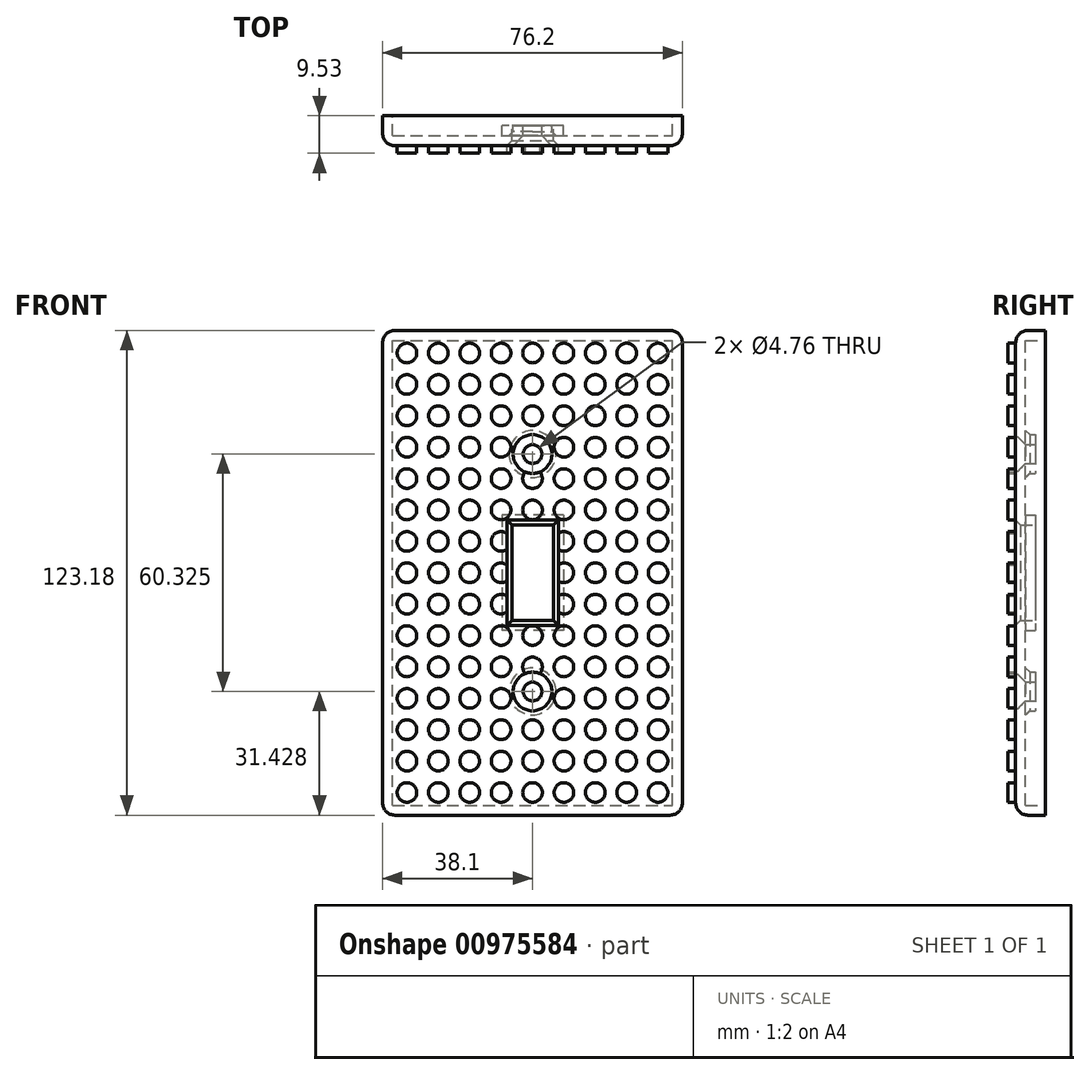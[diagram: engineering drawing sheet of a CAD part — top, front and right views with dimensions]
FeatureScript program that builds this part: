
annotation { "Feature Type Name" : "Feature", "Feature Type Description" : "" }
export const myFeature = defineFeature(function(context is Context, id is Id, definition is map)
    precondition{}
    {
        {
            var Q0;
            Q0=qCreatedBy(makeId("Front.planeOp"),FACE);
            var sketch = newSketch(context, id + "F0", { "sketchPlane" : qUnion([Q0])});
            skLineSegment(sketch, "E0.bottom", {"start": v(-38.1, -61.6) * mm, "end": v(38.1, -61.6) * mm});
            skLineSegment(sketch, "E0.top", {"start": v(-38.1, 61.6) * mm, "end": v(38.1, 61.6) * mm});
            skLineSegment(sketch, "E0.left", {"start": v(-38.1, -61.6) * mm, "end": v(-38.1, 61.6) * mm});
            skLineSegment(sketch, "E0.right", {"start": v(38.1, -61.6) * mm, "end": v(38.1, 61.6) * mm});
            skPoint(sketch, "E0.middle", {"position": v(0, 0) * mm});
            skLineSegment(sketch, "E1", {"start": v(0, 61.6) * mm, "end": v(0, -61.6) * mm, "construction": true});
            skLineSegment(sketch, "E2", {"start": v(-38.1, 0) * mm, "end": v(38.1, 0) * mm, "construction": true});
            skLineSegment(sketch, "E3", {"start": v(22.96, 61.6) * mm, "end": v(22.96, -61.6) * mm, "construction": true});
            skPoint(sketch, "E4.middle", {"position": v(22.96, 0) * mm});
            skLineSegment(sketch, "E5.bottom", {"start": v(-5.27, -12.13) * mm, "end": v(5.27, -12.13) * mm});
            skLineSegment(sketch, "E5.top", {"start": v(-5.27, 12.13) * mm, "end": v(5.27, 12.13) * mm});
            skLineSegment(sketch, "E5.left", {"start": v(-5.27, -12.13) * mm, "end": v(-5.27, 12.13) * mm});
            skLineSegment(sketch, "E5.right", {"start": v(5.27, -12.13) * mm, "end": v(5.27, 12.13) * mm});
            skCircle(sketch, "E6", {"center": v(0, -30.16) * mm, "radius": 2.38 * mm});
            skCircle(sketch, "E7.MirrorC", {"center": v(0, 30.16) * mm, "radius": 2.38 * mm});
            skSolve(sketch);
        }
        {
            var Q0;
            Q0=makeQuery(id+"F0.imprint","IMPRINT",FACE,{"disambiguationData":[TD([[makeQuery(id+"F0.imprint","IMPRINT",EDGE,{"derivedFrom":sQuery(id+"F0.wireOp",EDGE,"E0.bottom")}),1.0]])]});
            extrude(context, id + "F1", {"entities" : qUnion([Q0]), "depth" : 7.62 * mm, "offsetDistance" : 25.4 * mm});
        }
        {
            var Q0;
            Q0=makeQuery(id+"F1.opExtrude","CAP_EDGE",EDGE,{"disambiguationData":[OSD([sQuery(id+"F0.wireOp",EDGE,"E7.MirrorC")])],"isStart":false});
            var Q1;
            Q1=makeQuery(id+"F1.opExtrude","CAP_EDGE",EDGE,{"disambiguationData":[OSD([sQuery(id+"F0.wireOp",EDGE,"E6")])],"isStart":false});
            chamfer(context, id + "F2", {"entities" : qUnion([Q0, Q1]), "width" : 2.54 * mm, "tangentPropagation" : true});
        }
        {
            var Q0;
            Q0=makeQuery(id+"F1.opExtrude","CAP_EDGE",EDGE,{"disambiguationData":[OSD([sQuery(id+"F0.wireOp",EDGE,"E5.bottom")])],"isStart":false});
            var Q1;
            Q1=makeQuery(id+"F1.opExtrude","CAP_EDGE",EDGE,{"disambiguationData":[OSD([sQuery(id+"F0.wireOp",EDGE,"E5.top")])],"isStart":false});
            var Q2;
            Q2=makeQuery(id+"F1.opExtrude","CAP_EDGE",EDGE,{"disambiguationData":[OSD([sQuery(id+"F0.wireOp",EDGE,"E5.right")])],"isStart":false});
            var Q3;
            Q3=makeQuery(id+"F1.opExtrude","CAP_EDGE",EDGE,{"disambiguationData":[OSD([sQuery(id+"F0.wireOp",EDGE,"E5.left")])],"isStart":false});
            chamfer(context, id + "F3", {"entities" : qUnion([Q0, Q1, Q2, Q3]), "width" : 1.27 * mm, "tangentPropagation" : true});
        }
        {
            var Q0;
            Q0=makeQuery(id+"F1.opExtrude","CAP_FACE",FACE,{"disambiguationData":[OSD([sQuery(id+"F0.wireOp",EDGE,"E0.bottom"),sQuery(id+"F0.wireOp",EDGE,"E0.top"),sQuery(id+"F0.wireOp",EDGE,"E0.left"),sQuery(id+"F0.wireOp",EDGE,"E0.right"),sQuery(id+"F0.wireOp",EDGE,"E4.bottom"),sQuery(id+"F0.wireOp",EDGE,"E4.top"),sQuery(id+"F0.wireOp",EDGE,"E4.left"),sQuery(id+"F0.wireOp",EDGE,"E4.right"),sQuery(id+"F0.wireOp",EDGE,"S8rWea5z-x2db-HdL8-dZlx-mBKRZtJuW5yt"),sQuery(id+"F0.wireOp",EDGE,"667eedda-f1dc-4c61-957f-706faf60f5200.MirrorC"),sQuery(id+"F0.wireOp",EDGE,"48815ae1-3f2c-4afa-9184-387e88e8cfc90.MirrorC"),sQuery(id+"F0.wireOp",EDGE,"5efa72a1-dbf9-4033-b1ce-7067f076b67a0.MirrorC"),sQuery(id+"F0.wireOp",EDGE,"e74374d9-3310-4d52-b099-d9de6480f7030.MirrorCS"),sQuery(id+"F0.wireOp",EDGE,"54ec0b88-7cfc-4447-87f8-6753f306d23d0.MirrorCS"),sQuery(id+"F0.wireOp",EDGE,"b89ad579-1ec3-48bc-a1ee-9315b749428f0.MirrorCS"),sQuery(id+"F0.wireOp",EDGE,"6356497d-8d2b-4f01-b385-a6d8bf8b30600.MirrorCS")])],"isStart":true});
            shell(context, id + "F4", {"entities" : qUnion([Q0]), "thickness" : 2.54 * mm});
        }
        {
            var Q0;
            {var subQ0=sQuery(id+"F0.wireOp",EDGE,"6356497d-8d2b-4f01-b385-a6d8bf8b30600.MirrorCS");var subQ1=sQuery(id+"F0.wireOp",EDGE,"b89ad579-1ec3-48bc-a1ee-9315b749428f0.MirrorCS");var subQ2=sQuery(id+"F0.wireOp",EDGE,"54ec0b88-7cfc-4447-87f8-6753f306d23d0.MirrorCS");var subQ3=sQuery(id+"F0.wireOp",EDGE,"e74374d9-3310-4d52-b099-d9de6480f7030.MirrorCS");var subQ4=sQuery(id+"F0.wireOp",EDGE,"5efa72a1-dbf9-4033-b1ce-7067f076b67a0.MirrorC");var subQ5=sQuery(id+"F0.wireOp",EDGE,"48815ae1-3f2c-4afa-9184-387e88e8cfc90.MirrorC");var subQ6=sQuery(id+"F0.wireOp",EDGE,"667eedda-f1dc-4c61-957f-706faf60f5200.MirrorC");var subQ7=sQuery(id+"F0.wireOp",EDGE,"S8rWea5z-x2db-HdL8-dZlx-mBKRZtJuW5yt");var subQ8=sQuery(id+"F0.wireOp",EDGE,"E4.right");var subQ9=sQuery(id+"F0.wireOp",EDGE,"E4.left");var subQ10=sQuery(id+"F0.wireOp",EDGE,"E4.top");var subQ11=sQuery(id+"F0.wireOp",EDGE,"E4.bottom");var subQ12=sQuery(id+"F0.wireOp",EDGE,"E0.right");var subQ13=sQuery(id+"F0.wireOp",EDGE,"E0.left");var subQ14=sQuery(id+"F0.wireOp",EDGE,"E0.top");var subQ15=sQuery(id+"F0.wireOp",EDGE,"E0.bottom");Q0=makeQuery(id+"F4.opShell","OFFSET_FACE",FACE,{"disambiguationData":[OSD([subQ15,subQ14,subQ13,subQ12,subQ11,subQ10,subQ9,subQ8,subQ7,subQ6,subQ5,subQ4,subQ3,subQ2,subQ1,subQ0]),TDD([makeQuery(id+"F1.opExtrude","CAP_FACE",FACE,{"disambiguationData":[OSD([subQ15,subQ14,subQ13,subQ12,subQ11,subQ10,subQ9,subQ8,subQ7,subQ6,subQ5,subQ4,subQ3,subQ2,subQ1,subQ0])],"isStart":true})]),OD(0.0)]});}
            var sketch = newSketch(context, id + "F5", { "sketchPlane" : qUnion([Q0])});
            skLineSegment(sketch, "E8.bottom", {"start": v(-28.58, -38.1) * mm, "end": v(28.58, -38.1) * mm});
            skLineSegment(sketch, "E8.top", {"start": v(-28.58, 38.1) * mm, "end": v(28.57, 38.1) * mm});
            skLineSegment(sketch, "E8.left", {"start": v(-28.58, -38.1) * mm, "end": v(-28.58, 38.1) * mm});
            skLineSegment(sketch, "E8.right", {"start": v(28.58, -38.1) * mm, "end": v(28.57, 38.1) * mm});
            skPoint(sketch, "E8.middle", {"position": v(0, 0) * mm});
            skSolve(sketch);
        }
        {
            var Q0;
            Q0=makeQuery(id+"F5.imprint","IMPRINT",FACE,{"disambiguationData":[TD([[makeQuery(id+"F5.imprint","IMPRINT",EDGE,{"derivedFrom":sQuery(id+"F5.wireOp",EDGE,"E8.bottom")}),1.0]])]});
            extrude(context, id + "F6", {"entities" : qUnion([Q0]), "operationType" : NewBodyOperationType.REMOVE, "oppositeDirection" : true, "depth" : 2.54 * mm, "offsetDistance" : 25.4 * mm});
        }
        {
            var Q0;
            Q0=makeQuery(id+"F1.opExtrude","SWEPT_EDGE",EDGE,{"disambiguationData":[OSD([sQuery(id+"F0.wireOp",EDGE,"E0.top"),sQuery(id+"F0.wireOp",EDGE,"E0.right")])]});
            var Q1;
            Q1=makeQuery(id+"F1.opExtrude","SWEPT_EDGE",EDGE,{"disambiguationData":[OSD([sQuery(id+"F0.wireOp",EDGE,"E0.bottom"),sQuery(id+"F0.wireOp",EDGE,"E0.right")])]});
            var Q2;
            Q2=makeQuery(id+"F1.opExtrude","SWEPT_EDGE",EDGE,{"disambiguationData":[OSD([sQuery(id+"F0.wireOp",EDGE,"E0.bottom"),sQuery(id+"F0.wireOp",EDGE,"E0.left")])]});
            var Q3;
            Q3=makeQuery(id+"F1.opExtrude","SWEPT_EDGE",EDGE,{"disambiguationData":[OSD([sQuery(id+"F0.wireOp",EDGE,"E0.top"),sQuery(id+"F0.wireOp",EDGE,"E0.left")])]});
            fillet(context, id + "F7", {"entities" : qUnion([Q0, Q1, Q2, Q3]), "radius" : 3.17 * mm, "tangentPropagation" : true, "allowEdgeOverflow" : false});
        }
        {
            var Q0;
            Q0=makeQuery(id+"F1.opExtrude","CAP_EDGE",EDGE,{"disambiguationData":[OSD([sQuery(id+"F0.wireOp",EDGE,"E0.top")])],"isStart":false});
            fillet(context, id + "F8", {"entities" : qUnion([Q0]), "radius" : 3.17 * mm, "tangentPropagation" : true, "allowEdgeOverflow" : false});
        }
        {
            var Q0;
            Q0=makeQuery(id+"F1.opExtrude","CAP_FACE",FACE,{"disambiguationData":[OSD([sQuery(id+"F0.wireOp",EDGE,"E0.bottom"),sQuery(id+"F0.wireOp",EDGE,"E0.top"),sQuery(id+"F0.wireOp",EDGE,"E0.left"),sQuery(id+"F0.wireOp",EDGE,"E0.right"),sQuery(id+"F0.wireOp",EDGE,"E5.bottom"),sQuery(id+"F0.wireOp",EDGE,"E5.top"),sQuery(id+"F0.wireOp",EDGE,"E5.left"),sQuery(id+"F0.wireOp",EDGE,"E5.right"),sQuery(id+"F0.wireOp",EDGE,"E6"),sQuery(id+"F0.wireOp",EDGE,"E7.MirrorC")])],"isStart":false});
            var sketch = newSketch(context, id + "F9", { "sketchPlane" : qUnion([Q0])});
            skCircle(sketch, "E9", {"center": v(0, 0) * mm, "radius": 2.49 * mm, "construction": true});
            skCircle(sketch, "E10.0.2.0", {"center": v(0, 15.95) * mm, "radius": 2.49 * mm});
            skCircle(sketch, "E10.0.3.0", {"center": v(0, 23.93) * mm, "radius": 2.49 * mm});
            skCircle(sketch, "E10.0.5.0", {"center": v(0, 39.88) * mm, "radius": 2.49 * mm});
            skCircle(sketch, "E10.0.6.0", {"center": v(0, 47.85) * mm, "radius": 2.49 * mm});
            skCircle(sketch, "E10.0.7.0", {"center": v(0, 55.83) * mm, "radius": 2.49 * mm});
            skCircle(sketch, "E10.1.0.0", {"center": v(7.98, 0) * mm, "radius": 2.49 * mm});
            skCircle(sketch, "E10.1.1.0", {"center": v(7.98, 7.98) * mm, "radius": 2.49 * mm});
            skCircle(sketch, "E10.1.2.0", {"center": v(7.98, 15.95) * mm, "radius": 2.49 * mm});
            skCircle(sketch, "E10.1.3.0", {"center": v(7.98, 23.93) * mm, "radius": 2.49 * mm});
            skCircle(sketch, "E10.1.4.0", {"center": v(7.98, 31.9) * mm, "radius": 2.49 * mm});
            skCircle(sketch, "E10.1.5.0", {"center": v(7.98, 39.88) * mm, "radius": 2.49 * mm});
            skCircle(sketch, "E10.1.6.0", {"center": v(7.98, 47.85) * mm, "radius": 2.49 * mm});
            skCircle(sketch, "E10.1.7.0", {"center": v(7.98, 55.83) * mm, "radius": 2.49 * mm});
            skCircle(sketch, "E10.2.0.0", {"center": v(15.95, 0) * mm, "radius": 2.49 * mm});
            skCircle(sketch, "E10.2.1.0", {"center": v(15.95, 7.98) * mm, "radius": 2.49 * mm});
            skCircle(sketch, "E10.2.2.0", {"center": v(15.95, 15.95) * mm, "radius": 2.49 * mm});
            skCircle(sketch, "E10.2.3.0", {"center": v(15.95, 23.93) * mm, "radius": 2.49 * mm});
            skCircle(sketch, "E10.2.4.0", {"center": v(15.95, 31.9) * mm, "radius": 2.49 * mm});
            skCircle(sketch, "E10.2.5.0", {"center": v(15.95, 39.88) * mm, "radius": 2.49 * mm});
            skCircle(sketch, "E10.2.6.0", {"center": v(15.95, 47.85) * mm, "radius": 2.49 * mm});
            skCircle(sketch, "E10.2.7.0", {"center": v(15.95, 55.83) * mm, "radius": 2.49 * mm});
            skCircle(sketch, "E10.3.0.0", {"center": v(23.93, 0) * mm, "radius": 2.49 * mm});
            skCircle(sketch, "E10.3.1.0", {"center": v(23.93, 7.98) * mm, "radius": 2.49 * mm});
            skCircle(sketch, "E10.3.2.0", {"center": v(23.93, 15.95) * mm, "radius": 2.49 * mm});
            skCircle(sketch, "E10.3.3.0", {"center": v(23.93, 23.93) * mm, "radius": 2.49 * mm});
            skCircle(sketch, "E10.3.4.0", {"center": v(23.93, 31.9) * mm, "radius": 2.49 * mm});
            skCircle(sketch, "E10.3.5.0", {"center": v(23.93, 39.88) * mm, "radius": 2.49 * mm});
            skCircle(sketch, "E10.3.6.0", {"center": v(23.93, 47.85) * mm, "radius": 2.49 * mm});
            skCircle(sketch, "E10.3.7.0", {"center": v(23.93, 55.83) * mm, "radius": 2.49 * mm});
            skCircle(sketch, "E10.4.0.0", {"center": v(31.9, 0) * mm, "radius": 2.49 * mm});
            skCircle(sketch, "E10.4.1.0", {"center": v(31.9, 7.98) * mm, "radius": 2.49 * mm});
            skCircle(sketch, "E10.4.2.0", {"center": v(31.9, 15.95) * mm, "radius": 2.49 * mm});
            skCircle(sketch, "E10.4.3.0", {"center": v(31.9, 23.93) * mm, "radius": 2.49 * mm});
            skCircle(sketch, "E10.4.4.0", {"center": v(31.9, 31.9) * mm, "radius": 2.49 * mm});
            skCircle(sketch, "E10.4.5.0", {"center": v(31.9, 39.88) * mm, "radius": 2.49 * mm});
            skCircle(sketch, "E10.4.6.0", {"center": v(31.9, 47.85) * mm, "radius": 2.49 * mm});
            skCircle(sketch, "E10.4.7.0", {"center": v(31.9, 55.83) * mm, "radius": 2.49 * mm});
            skLineSegment(sketch, "E10.direction1", {"start": v(0, 0) * mm, "end": v(7.98, 0) * mm, "construction": true});
            skLineSegment(sketch, "E10.direction2", {"start": v(0, 0) * mm, "end": v(0, 7.98) * mm, "construction": true});
            skCircle(sketch, "E11.0.1.0", {"center": v(-7.98, 0) * mm, "radius": 2.49 * mm});
            skCircle(sketch, "E11.0.2.0", {"center": v(-15.95, 0) * mm, "radius": 2.49 * mm});
            skCircle(sketch, "E11.0.3.0", {"center": v(-23.93, 0) * mm, "radius": 2.49 * mm});
            skCircle(sketch, "E11.0.4.0", {"center": v(-31.9, 0) * mm, "radius": 2.49 * mm});
            skCircle(sketch, "E11.1.1.0", {"center": v(-7.98, -7.98) * mm, "radius": 2.49 * mm});
            skCircle(sketch, "E11.1.2.0", {"center": v(-15.95, -7.98) * mm, "radius": 2.49 * mm});
            skCircle(sketch, "E11.1.3.0", {"center": v(-23.93, -7.98) * mm, "radius": 2.49 * mm});
            skCircle(sketch, "E11.1.4.0", {"center": v(-31.9, -7.98) * mm, "radius": 2.49 * mm});
            skCircle(sketch, "E11.2.0.0", {"center": v(0, -15.95) * mm, "radius": 2.49 * mm});
            skCircle(sketch, "E11.2.1.0", {"center": v(-7.98, -15.95) * mm, "radius": 2.49 * mm});
            skCircle(sketch, "E11.2.2.0", {"center": v(-15.95, -15.95) * mm, "radius": 2.49 * mm});
            skCircle(sketch, "E11.2.3.0", {"center": v(-23.93, -15.95) * mm, "radius": 2.49 * mm});
            skCircle(sketch, "E11.2.4.0", {"center": v(-31.9, -15.95) * mm, "radius": 2.49 * mm});
            skCircle(sketch, "E11.3.0.0", {"center": v(0, -23.93) * mm, "radius": 2.49 * mm});
            skCircle(sketch, "E11.3.1.0", {"center": v(-7.98, -23.93) * mm, "radius": 2.49 * mm});
            skCircle(sketch, "E11.3.2.0", {"center": v(-15.95, -23.93) * mm, "radius": 2.49 * mm});
            skCircle(sketch, "E11.3.3.0", {"center": v(-23.93, -23.93) * mm, "radius": 2.49 * mm});
            skCircle(sketch, "E11.3.4.0", {"center": v(-31.9, -23.93) * mm, "radius": 2.49 * mm});
            skCircle(sketch, "E11.4.1.0", {"center": v(-7.98, -31.9) * mm, "radius": 2.49 * mm});
            skCircle(sketch, "E11.4.2.0", {"center": v(-15.95, -31.9) * mm, "radius": 2.49 * mm});
            skCircle(sketch, "E11.4.3.0", {"center": v(-23.93, -31.9) * mm, "radius": 2.49 * mm});
            skCircle(sketch, "E11.4.4.0", {"center": v(-31.9, -31.9) * mm, "radius": 2.49 * mm});
            skCircle(sketch, "E11.5.0.0", {"center": v(0, -39.88) * mm, "radius": 2.49 * mm});
            skCircle(sketch, "E11.5.1.0", {"center": v(-7.98, -39.88) * mm, "radius": 2.49 * mm});
            skCircle(sketch, "E11.5.2.0", {"center": v(-15.95, -39.88) * mm, "radius": 2.49 * mm});
            skCircle(sketch, "E11.5.3.0", {"center": v(-23.93, -39.88) * mm, "radius": 2.49 * mm});
            skCircle(sketch, "E11.5.4.0", {"center": v(-31.9, -39.88) * mm, "radius": 2.49 * mm});
            skCircle(sketch, "E11.6.0.0", {"center": v(0, -47.85) * mm, "radius": 2.49 * mm});
            skCircle(sketch, "E11.6.1.0", {"center": v(-7.98, -47.85) * mm, "radius": 2.49 * mm});
            skCircle(sketch, "E11.6.2.0", {"center": v(-15.95, -47.85) * mm, "radius": 2.49 * mm});
            skCircle(sketch, "E11.6.3.0", {"center": v(-23.93, -47.85) * mm, "radius": 2.49 * mm});
            skCircle(sketch, "E11.6.4.0", {"center": v(-31.9, -47.85) * mm, "radius": 2.49 * mm});
            skCircle(sketch, "E11.7.0.0", {"center": v(0, -55.83) * mm, "radius": 2.49 * mm});
            skCircle(sketch, "E11.7.1.0", {"center": v(-7.98, -55.83) * mm, "radius": 2.49 * mm});
            skCircle(sketch, "E11.7.2.0", {"center": v(-15.95, -55.83) * mm, "radius": 2.49 * mm});
            skCircle(sketch, "E11.7.3.0", {"center": v(-23.93, -55.83) * mm, "radius": 2.49 * mm});
            skCircle(sketch, "E11.7.4.0", {"center": v(-31.9, -55.83) * mm, "radius": 2.49 * mm});
            skLineSegment(sketch, "E11.direction1", {"start": v(0, 0) * mm, "end": v(0, -7.98) * mm, "construction": true});
            skLineSegment(sketch, "E11.direction2", {"start": v(0, 0) * mm, "end": v(-7.98, 0) * mm, "construction": true});
            skCircle(sketch, "E12.1.1.0", {"center": v(-7.98, 7.98) * mm, "radius": 2.49 * mm});
            skCircle(sketch, "E12.1.2.0", {"center": v(-7.98, 15.95) * mm, "radius": 2.49 * mm});
            skCircle(sketch, "E12.1.3.0", {"center": v(-7.98, 23.93) * mm, "radius": 2.49 * mm});
            skCircle(sketch, "E12.1.4.0", {"center": v(-7.98, 31.9) * mm, "radius": 2.49 * mm});
            skCircle(sketch, "E12.1.5.0", {"center": v(-7.98, 39.88) * mm, "radius": 2.49 * mm});
            skCircle(sketch, "E12.1.6.0", {"center": v(-7.98, 47.85) * mm, "radius": 2.49 * mm});
            skCircle(sketch, "E12.1.7.0", {"center": v(-7.98, 55.83) * mm, "radius": 2.49 * mm});
            skCircle(sketch, "E12.2.1.0", {"center": v(-15.95, 7.98) * mm, "radius": 2.49 * mm});
            skCircle(sketch, "E12.2.2.0", {"center": v(-15.95, 15.95) * mm, "radius": 2.49 * mm});
            skCircle(sketch, "E12.2.3.0", {"center": v(-15.95, 23.93) * mm, "radius": 2.49 * mm});
            skCircle(sketch, "E12.2.4.0", {"center": v(-15.95, 31.9) * mm, "radius": 2.49 * mm});
            skCircle(sketch, "E12.2.5.0", {"center": v(-15.95, 39.88) * mm, "radius": 2.49 * mm});
            skCircle(sketch, "E12.2.6.0", {"center": v(-15.95, 47.85) * mm, "radius": 2.49 * mm});
            skCircle(sketch, "E12.2.7.0", {"center": v(-15.95, 55.83) * mm, "radius": 2.49 * mm});
            skCircle(sketch, "E12.3.1.0", {"center": v(-23.93, 7.98) * mm, "radius": 2.49 * mm});
            skCircle(sketch, "E12.3.2.0", {"center": v(-23.93, 15.95) * mm, "radius": 2.49 * mm});
            skCircle(sketch, "E12.3.3.0", {"center": v(-23.93, 23.93) * mm, "radius": 2.49 * mm});
            skCircle(sketch, "E12.3.4.0", {"center": v(-23.93, 31.9) * mm, "radius": 2.49 * mm});
            skCircle(sketch, "E12.3.5.0", {"center": v(-23.93, 39.88) * mm, "radius": 2.49 * mm});
            skCircle(sketch, "E12.3.6.0", {"center": v(-23.93, 47.85) * mm, "radius": 2.49 * mm});
            skCircle(sketch, "E12.3.7.0", {"center": v(-23.93, 55.83) * mm, "radius": 2.49 * mm});
            skCircle(sketch, "E12.4.1.0", {"center": v(-31.9, 7.98) * mm, "radius": 2.49 * mm});
            skCircle(sketch, "E12.4.2.0", {"center": v(-31.9, 15.95) * mm, "radius": 2.49 * mm});
            skCircle(sketch, "E12.4.3.0", {"center": v(-31.9, 23.93) * mm, "radius": 2.49 * mm});
            skCircle(sketch, "E12.4.4.0", {"center": v(-31.9, 31.9) * mm, "radius": 2.49 * mm});
            skCircle(sketch, "E12.4.5.0", {"center": v(-31.9, 39.88) * mm, "radius": 2.49 * mm});
            skCircle(sketch, "E12.4.6.0", {"center": v(-31.9, 47.85) * mm, "radius": 2.49 * mm});
            skCircle(sketch, "E12.4.7.0", {"center": v(-31.9, 55.83) * mm, "radius": 2.49 * mm});
            skCircle(sketch, "E13.1.1.0", {"center": v(7.98, -7.98) * mm, "radius": 2.49 * mm});
            skCircle(sketch, "E13.1.2.0", {"center": v(7.98, -15.95) * mm, "radius": 2.49 * mm});
            skCircle(sketch, "E13.1.3.0", {"center": v(7.98, -23.93) * mm, "radius": 2.49 * mm});
            skCircle(sketch, "E13.1.4.0", {"center": v(7.98, -31.9) * mm, "radius": 2.49 * mm});
            skCircle(sketch, "E13.1.5.0", {"center": v(7.98, -39.88) * mm, "radius": 2.49 * mm});
            skCircle(sketch, "E13.1.6.0", {"center": v(7.98, -47.85) * mm, "radius": 2.49 * mm});
            skCircle(sketch, "E13.1.7.0", {"center": v(7.98, -55.83) * mm, "radius": 2.49 * mm});
            skCircle(sketch, "E13.2.1.0", {"center": v(15.95, -7.98) * mm, "radius": 2.49 * mm});
            skCircle(sketch, "E13.2.2.0", {"center": v(15.95, -15.95) * mm, "radius": 2.49 * mm});
            skCircle(sketch, "E13.2.3.0", {"center": v(15.95, -23.93) * mm, "radius": 2.49 * mm});
            skCircle(sketch, "E13.2.4.0", {"center": v(15.95, -31.9) * mm, "radius": 2.49 * mm});
            skCircle(sketch, "E13.2.5.0", {"center": v(15.95, -39.88) * mm, "radius": 2.49 * mm});
            skCircle(sketch, "E13.2.6.0", {"center": v(15.95, -47.85) * mm, "radius": 2.49 * mm});
            skCircle(sketch, "E13.2.7.0", {"center": v(15.95, -55.83) * mm, "radius": 2.49 * mm});
            skCircle(sketch, "E13.3.1.0", {"center": v(23.93, -7.98) * mm, "radius": 2.49 * mm});
            skCircle(sketch, "E13.3.2.0", {"center": v(23.93, -15.95) * mm, "radius": 2.49 * mm});
            skCircle(sketch, "E13.3.3.0", {"center": v(23.93, -23.93) * mm, "radius": 2.49 * mm});
            skCircle(sketch, "E13.3.4.0", {"center": v(23.93, -31.9) * mm, "radius": 2.49 * mm});
            skCircle(sketch, "E13.3.5.0", {"center": v(23.93, -39.88) * mm, "radius": 2.49 * mm});
            skCircle(sketch, "E13.3.6.0", {"center": v(23.93, -47.85) * mm, "radius": 2.49 * mm});
            skCircle(sketch, "E13.3.7.0", {"center": v(23.93, -55.83) * mm, "radius": 2.49 * mm});
            skCircle(sketch, "E13.4.1.0", {"center": v(31.9, -7.98) * mm, "radius": 2.49 * mm});
            skCircle(sketch, "E13.4.2.0", {"center": v(31.9, -15.95) * mm, "radius": 2.49 * mm});
            skCircle(sketch, "E13.4.3.0", {"center": v(31.9, -23.93) * mm, "radius": 2.49 * mm});
            skCircle(sketch, "E13.4.4.0", {"center": v(31.9, -31.9) * mm, "radius": 2.49 * mm});
            skCircle(sketch, "E13.4.5.0", {"center": v(31.9, -39.88) * mm, "radius": 2.49 * mm});
            skCircle(sketch, "E13.4.6.0", {"center": v(31.9, -47.85) * mm, "radius": 2.49 * mm});
            skCircle(sketch, "E13.4.7.0", {"center": v(31.9, -55.83) * mm, "radius": 2.49 * mm});
            skSolve(sketch);
        }
        {
            var Q0;
            {var subQ0=sQuery(id+"F9.wireOp",EDGE,"E12.4.7.0");var subQ1=sQuery(id+"F0.wireOp",EDGE,"E0.left");var subQ2=makeQuery(id+"F8.opFillet","BLEND_EDGE",EDGE,{"blendedFrom":[makeQuery(id+"F1.opExtrude","CAP_EDGE",EDGE,{"disambiguationData":[OSD([subQ1])],"isStart":false}),makeQuery(id+"F1.opExtrude","CAP_FACE",FACE,{"disambiguationData":[OSD([sQuery(id+"F0.wireOp",EDGE,"E0.bottom"),sQuery(id+"F0.wireOp",EDGE,"E0.top"),subQ1,sQuery(id+"F0.wireOp",EDGE,"E0.right"),sQuery(id+"F0.wireOp",EDGE,"E5.bottom"),sQuery(id+"F0.wireOp",EDGE,"E5.top"),sQuery(id+"F0.wireOp",EDGE,"E5.left"),sQuery(id+"F0.wireOp",EDGE,"E5.right"),sQuery(id+"F0.wireOp",EDGE,"E6"),sQuery(id+"F0.wireOp",EDGE,"E7.MirrorC")])],"isStart":false})],"blendedInto":[makeQuery(id+"F1.opExtrude","CAP_FACE",FACE,{"disambiguationData":[OSD([sQuery(id+"F0.wireOp",EDGE,"E0.bottom"),sQuery(id+"F0.wireOp",EDGE,"E0.top"),subQ1,sQuery(id+"F0.wireOp",EDGE,"E0.right"),sQuery(id+"F0.wireOp",EDGE,"E5.bottom"),sQuery(id+"F0.wireOp",EDGE,"E5.top"),sQuery(id+"F0.wireOp",EDGE,"E5.left"),sQuery(id+"F0.wireOp",EDGE,"E5.right"),sQuery(id+"F0.wireOp",EDGE,"E6"),sQuery(id+"F0.wireOp",EDGE,"E7.MirrorC")])],"isStart":false})]});var subQ3=makeQuery(id+"F9.imprint","INTERSECT",VERTEX,{"disambiguationData":[OD(0.0)],"derivedFrom":[subQ2,subQ0]});Q0=makeQuery(id+"F9.imprint","IMPRINT",FACE,{"disambiguationData":[TD([[makeQuery(id+"F9.imprint","IMPRINT",EDGE,{"disambiguationData":[TD([[subQ3,1.0]])],"derivedFrom":subQ0}),1.0]])]});}
            var Q1;
            {var subQ0=sQuery(id+"F9.wireOp",EDGE,"E12.4.6.0");var subQ1=sQuery(id+"F0.wireOp",EDGE,"E0.left");var subQ2=makeQuery(id+"F8.opFillet","BLEND_EDGE",EDGE,{"blendedFrom":[makeQuery(id+"F1.opExtrude","CAP_EDGE",EDGE,{"disambiguationData":[OSD([subQ1])],"isStart":false}),makeQuery(id+"F1.opExtrude","CAP_FACE",FACE,{"disambiguationData":[OSD([sQuery(id+"F0.wireOp",EDGE,"E0.bottom"),sQuery(id+"F0.wireOp",EDGE,"E0.top"),subQ1,sQuery(id+"F0.wireOp",EDGE,"E0.right"),sQuery(id+"F0.wireOp",EDGE,"E5.bottom"),sQuery(id+"F0.wireOp",EDGE,"E5.top"),sQuery(id+"F0.wireOp",EDGE,"E5.left"),sQuery(id+"F0.wireOp",EDGE,"E5.right"),sQuery(id+"F0.wireOp",EDGE,"E6"),sQuery(id+"F0.wireOp",EDGE,"E7.MirrorC")])],"isStart":false})],"blendedInto":[makeQuery(id+"F1.opExtrude","CAP_FACE",FACE,{"disambiguationData":[OSD([sQuery(id+"F0.wireOp",EDGE,"E0.bottom"),sQuery(id+"F0.wireOp",EDGE,"E0.top"),subQ1,sQuery(id+"F0.wireOp",EDGE,"E0.right"),sQuery(id+"F0.wireOp",EDGE,"E5.bottom"),sQuery(id+"F0.wireOp",EDGE,"E5.top"),sQuery(id+"F0.wireOp",EDGE,"E5.left"),sQuery(id+"F0.wireOp",EDGE,"E5.right"),sQuery(id+"F0.wireOp",EDGE,"E6"),sQuery(id+"F0.wireOp",EDGE,"E7.MirrorC")])],"isStart":false})]});var subQ3=makeQuery(id+"F9.imprint","INTERSECT",VERTEX,{"disambiguationData":[OD(0.0)],"derivedFrom":[subQ2,subQ0]});Q1=makeQuery(id+"F9.imprint","IMPRINT",FACE,{"disambiguationData":[TD([[makeQuery(id+"F9.imprint","IMPRINT",EDGE,{"disambiguationData":[TD([[subQ3,1.0]])],"derivedFrom":subQ0}),1.0]])]});}
            var Q2;
            {var subQ0=sQuery(id+"F9.wireOp",EDGE,"E12.4.5.0");var subQ1=sQuery(id+"F0.wireOp",EDGE,"E0.left");var subQ2=makeQuery(id+"F8.opFillet","BLEND_EDGE",EDGE,{"blendedFrom":[makeQuery(id+"F1.opExtrude","CAP_EDGE",EDGE,{"disambiguationData":[OSD([subQ1])],"isStart":false}),makeQuery(id+"F1.opExtrude","CAP_FACE",FACE,{"disambiguationData":[OSD([sQuery(id+"F0.wireOp",EDGE,"E0.bottom"),sQuery(id+"F0.wireOp",EDGE,"E0.top"),subQ1,sQuery(id+"F0.wireOp",EDGE,"E0.right"),sQuery(id+"F0.wireOp",EDGE,"E5.bottom"),sQuery(id+"F0.wireOp",EDGE,"E5.top"),sQuery(id+"F0.wireOp",EDGE,"E5.left"),sQuery(id+"F0.wireOp",EDGE,"E5.right"),sQuery(id+"F0.wireOp",EDGE,"E6"),sQuery(id+"F0.wireOp",EDGE,"E7.MirrorC")])],"isStart":false})],"blendedInto":[makeQuery(id+"F1.opExtrude","CAP_FACE",FACE,{"disambiguationData":[OSD([sQuery(id+"F0.wireOp",EDGE,"E0.bottom"),sQuery(id+"F0.wireOp",EDGE,"E0.top"),subQ1,sQuery(id+"F0.wireOp",EDGE,"E0.right"),sQuery(id+"F0.wireOp",EDGE,"E5.bottom"),sQuery(id+"F0.wireOp",EDGE,"E5.top"),sQuery(id+"F0.wireOp",EDGE,"E5.left"),sQuery(id+"F0.wireOp",EDGE,"E5.right"),sQuery(id+"F0.wireOp",EDGE,"E6"),sQuery(id+"F0.wireOp",EDGE,"E7.MirrorC")])],"isStart":false})]});var subQ3=makeQuery(id+"F9.imprint","INTERSECT",VERTEX,{"disambiguationData":[OD(0.0)],"derivedFrom":[subQ2,subQ0]});Q2=makeQuery(id+"F9.imprint","IMPRINT",FACE,{"disambiguationData":[TD([[makeQuery(id+"F9.imprint","IMPRINT",EDGE,{"disambiguationData":[TD([[subQ3,1.0]])],"derivedFrom":subQ0}),1.0]])]});}
            var Q3;
            {var subQ0=sQuery(id+"F9.wireOp",EDGE,"E12.4.4.0");var subQ1=sQuery(id+"F0.wireOp",EDGE,"E0.left");var subQ2=makeQuery(id+"F8.opFillet","BLEND_EDGE",EDGE,{"blendedFrom":[makeQuery(id+"F1.opExtrude","CAP_EDGE",EDGE,{"disambiguationData":[OSD([subQ1])],"isStart":false}),makeQuery(id+"F1.opExtrude","CAP_FACE",FACE,{"disambiguationData":[OSD([sQuery(id+"F0.wireOp",EDGE,"E0.bottom"),sQuery(id+"F0.wireOp",EDGE,"E0.top"),subQ1,sQuery(id+"F0.wireOp",EDGE,"E0.right"),sQuery(id+"F0.wireOp",EDGE,"E5.bottom"),sQuery(id+"F0.wireOp",EDGE,"E5.top"),sQuery(id+"F0.wireOp",EDGE,"E5.left"),sQuery(id+"F0.wireOp",EDGE,"E5.right"),sQuery(id+"F0.wireOp",EDGE,"E6"),sQuery(id+"F0.wireOp",EDGE,"E7.MirrorC")])],"isStart":false})],"blendedInto":[makeQuery(id+"F1.opExtrude","CAP_FACE",FACE,{"disambiguationData":[OSD([sQuery(id+"F0.wireOp",EDGE,"E0.bottom"),sQuery(id+"F0.wireOp",EDGE,"E0.top"),subQ1,sQuery(id+"F0.wireOp",EDGE,"E0.right"),sQuery(id+"F0.wireOp",EDGE,"E5.bottom"),sQuery(id+"F0.wireOp",EDGE,"E5.top"),sQuery(id+"F0.wireOp",EDGE,"E5.left"),sQuery(id+"F0.wireOp",EDGE,"E5.right"),sQuery(id+"F0.wireOp",EDGE,"E6"),sQuery(id+"F0.wireOp",EDGE,"E7.MirrorC")])],"isStart":false})]});var subQ3=makeQuery(id+"F9.imprint","INTERSECT",VERTEX,{"disambiguationData":[OD(0.0)],"derivedFrom":[subQ2,subQ0]});Q3=makeQuery(id+"F9.imprint","IMPRINT",FACE,{"disambiguationData":[TD([[makeQuery(id+"F9.imprint","IMPRINT",EDGE,{"disambiguationData":[TD([[subQ3,1.0]])],"derivedFrom":subQ0}),1.0]])]});}
            var Q4;
            {var subQ0=sQuery(id+"F9.wireOp",EDGE,"E12.4.3.0");var subQ1=sQuery(id+"F0.wireOp",EDGE,"E0.left");var subQ2=makeQuery(id+"F8.opFillet","BLEND_EDGE",EDGE,{"blendedFrom":[makeQuery(id+"F1.opExtrude","CAP_EDGE",EDGE,{"disambiguationData":[OSD([subQ1])],"isStart":false}),makeQuery(id+"F1.opExtrude","CAP_FACE",FACE,{"disambiguationData":[OSD([sQuery(id+"F0.wireOp",EDGE,"E0.bottom"),sQuery(id+"F0.wireOp",EDGE,"E0.top"),subQ1,sQuery(id+"F0.wireOp",EDGE,"E0.right"),sQuery(id+"F0.wireOp",EDGE,"E5.bottom"),sQuery(id+"F0.wireOp",EDGE,"E5.top"),sQuery(id+"F0.wireOp",EDGE,"E5.left"),sQuery(id+"F0.wireOp",EDGE,"E5.right"),sQuery(id+"F0.wireOp",EDGE,"E6"),sQuery(id+"F0.wireOp",EDGE,"E7.MirrorC")])],"isStart":false})],"blendedInto":[makeQuery(id+"F1.opExtrude","CAP_FACE",FACE,{"disambiguationData":[OSD([sQuery(id+"F0.wireOp",EDGE,"E0.bottom"),sQuery(id+"F0.wireOp",EDGE,"E0.top"),subQ1,sQuery(id+"F0.wireOp",EDGE,"E0.right"),sQuery(id+"F0.wireOp",EDGE,"E5.bottom"),sQuery(id+"F0.wireOp",EDGE,"E5.top"),sQuery(id+"F0.wireOp",EDGE,"E5.left"),sQuery(id+"F0.wireOp",EDGE,"E5.right"),sQuery(id+"F0.wireOp",EDGE,"E6"),sQuery(id+"F0.wireOp",EDGE,"E7.MirrorC")])],"isStart":false})]});var subQ3=makeQuery(id+"F9.imprint","INTERSECT",VERTEX,{"disambiguationData":[OD(0.0)],"derivedFrom":[subQ2,subQ0]});Q4=makeQuery(id+"F9.imprint","IMPRINT",FACE,{"disambiguationData":[TD([[makeQuery(id+"F9.imprint","IMPRINT",EDGE,{"disambiguationData":[TD([[subQ3,1.0]])],"derivedFrom":subQ0}),1.0]])]});}
            var Q5;
            {var subQ0=sQuery(id+"F9.wireOp",EDGE,"E12.4.2.0");var subQ1=sQuery(id+"F0.wireOp",EDGE,"E0.left");var subQ2=makeQuery(id+"F8.opFillet","BLEND_EDGE",EDGE,{"blendedFrom":[makeQuery(id+"F1.opExtrude","CAP_EDGE",EDGE,{"disambiguationData":[OSD([subQ1])],"isStart":false}),makeQuery(id+"F1.opExtrude","CAP_FACE",FACE,{"disambiguationData":[OSD([sQuery(id+"F0.wireOp",EDGE,"E0.bottom"),sQuery(id+"F0.wireOp",EDGE,"E0.top"),subQ1,sQuery(id+"F0.wireOp",EDGE,"E0.right"),sQuery(id+"F0.wireOp",EDGE,"E5.bottom"),sQuery(id+"F0.wireOp",EDGE,"E5.top"),sQuery(id+"F0.wireOp",EDGE,"E5.left"),sQuery(id+"F0.wireOp",EDGE,"E5.right"),sQuery(id+"F0.wireOp",EDGE,"E6"),sQuery(id+"F0.wireOp",EDGE,"E7.MirrorC")])],"isStart":false})],"blendedInto":[makeQuery(id+"F1.opExtrude","CAP_FACE",FACE,{"disambiguationData":[OSD([sQuery(id+"F0.wireOp",EDGE,"E0.bottom"),sQuery(id+"F0.wireOp",EDGE,"E0.top"),subQ1,sQuery(id+"F0.wireOp",EDGE,"E0.right"),sQuery(id+"F0.wireOp",EDGE,"E5.bottom"),sQuery(id+"F0.wireOp",EDGE,"E5.top"),sQuery(id+"F0.wireOp",EDGE,"E5.left"),sQuery(id+"F0.wireOp",EDGE,"E5.right"),sQuery(id+"F0.wireOp",EDGE,"E6"),sQuery(id+"F0.wireOp",EDGE,"E7.MirrorC")])],"isStart":false})]});var subQ3=makeQuery(id+"F9.imprint","INTERSECT",VERTEX,{"disambiguationData":[OD(0.0)],"derivedFrom":[subQ2,subQ0]});Q5=makeQuery(id+"F9.imprint","IMPRINT",FACE,{"disambiguationData":[TD([[makeQuery(id+"F9.imprint","IMPRINT",EDGE,{"disambiguationData":[TD([[subQ3,1.0]])],"derivedFrom":subQ0}),1.0]])]});}
            var Q6;
            {var subQ0=sQuery(id+"F9.wireOp",EDGE,"E12.4.1.0");var subQ1=sQuery(id+"F0.wireOp",EDGE,"E0.left");var subQ2=makeQuery(id+"F8.opFillet","BLEND_EDGE",EDGE,{"blendedFrom":[makeQuery(id+"F1.opExtrude","CAP_EDGE",EDGE,{"disambiguationData":[OSD([subQ1])],"isStart":false}),makeQuery(id+"F1.opExtrude","CAP_FACE",FACE,{"disambiguationData":[OSD([sQuery(id+"F0.wireOp",EDGE,"E0.bottom"),sQuery(id+"F0.wireOp",EDGE,"E0.top"),subQ1,sQuery(id+"F0.wireOp",EDGE,"E0.right"),sQuery(id+"F0.wireOp",EDGE,"E5.bottom"),sQuery(id+"F0.wireOp",EDGE,"E5.top"),sQuery(id+"F0.wireOp",EDGE,"E5.left"),sQuery(id+"F0.wireOp",EDGE,"E5.right"),sQuery(id+"F0.wireOp",EDGE,"E6"),sQuery(id+"F0.wireOp",EDGE,"E7.MirrorC")])],"isStart":false})],"blendedInto":[makeQuery(id+"F1.opExtrude","CAP_FACE",FACE,{"disambiguationData":[OSD([sQuery(id+"F0.wireOp",EDGE,"E0.bottom"),sQuery(id+"F0.wireOp",EDGE,"E0.top"),subQ1,sQuery(id+"F0.wireOp",EDGE,"E0.right"),sQuery(id+"F0.wireOp",EDGE,"E5.bottom"),sQuery(id+"F0.wireOp",EDGE,"E5.top"),sQuery(id+"F0.wireOp",EDGE,"E5.left"),sQuery(id+"F0.wireOp",EDGE,"E5.right"),sQuery(id+"F0.wireOp",EDGE,"E6"),sQuery(id+"F0.wireOp",EDGE,"E7.MirrorC")])],"isStart":false})]});var subQ3=makeQuery(id+"F9.imprint","INTERSECT",VERTEX,{"disambiguationData":[OD(0.0)],"derivedFrom":[subQ2,subQ0]});Q6=makeQuery(id+"F9.imprint","IMPRINT",FACE,{"disambiguationData":[TD([[makeQuery(id+"F9.imprint","IMPRINT",EDGE,{"disambiguationData":[TD([[subQ3,1.0]])],"derivedFrom":subQ0}),1.0]])]});}
            var Q7;
            {var subQ0=sQuery(id+"F9.wireOp",EDGE,"E11.0.4.0");var subQ1=sQuery(id+"F0.wireOp",EDGE,"E0.left");var subQ2=makeQuery(id+"F8.opFillet","BLEND_EDGE",EDGE,{"blendedFrom":[makeQuery(id+"F1.opExtrude","CAP_EDGE",EDGE,{"disambiguationData":[OSD([subQ1])],"isStart":false}),makeQuery(id+"F1.opExtrude","CAP_FACE",FACE,{"disambiguationData":[OSD([sQuery(id+"F0.wireOp",EDGE,"E0.bottom"),sQuery(id+"F0.wireOp",EDGE,"E0.top"),subQ1,sQuery(id+"F0.wireOp",EDGE,"E0.right"),sQuery(id+"F0.wireOp",EDGE,"E5.bottom"),sQuery(id+"F0.wireOp",EDGE,"E5.top"),sQuery(id+"F0.wireOp",EDGE,"E5.left"),sQuery(id+"F0.wireOp",EDGE,"E5.right"),sQuery(id+"F0.wireOp",EDGE,"E6"),sQuery(id+"F0.wireOp",EDGE,"E7.MirrorC")])],"isStart":false})],"blendedInto":[makeQuery(id+"F1.opExtrude","CAP_FACE",FACE,{"disambiguationData":[OSD([sQuery(id+"F0.wireOp",EDGE,"E0.bottom"),sQuery(id+"F0.wireOp",EDGE,"E0.top"),subQ1,sQuery(id+"F0.wireOp",EDGE,"E0.right"),sQuery(id+"F0.wireOp",EDGE,"E5.bottom"),sQuery(id+"F0.wireOp",EDGE,"E5.top"),sQuery(id+"F0.wireOp",EDGE,"E5.left"),sQuery(id+"F0.wireOp",EDGE,"E5.right"),sQuery(id+"F0.wireOp",EDGE,"E6"),sQuery(id+"F0.wireOp",EDGE,"E7.MirrorC")])],"isStart":false})]});var subQ3=makeQuery(id+"F9.imprint","INTERSECT",VERTEX,{"disambiguationData":[OD(0.0)],"derivedFrom":[subQ2,subQ0]});Q7=makeQuery(id+"F9.imprint","IMPRINT",FACE,{"disambiguationData":[TD([[makeQuery(id+"F9.imprint","IMPRINT",EDGE,{"disambiguationData":[TD([[subQ3,-1.0]])],"derivedFrom":subQ0}),1.0]])]});}
            var Q8;
            {var subQ0=sQuery(id+"F9.wireOp",EDGE,"E11.1.4.0");var subQ1=sQuery(id+"F0.wireOp",EDGE,"E0.left");var subQ2=makeQuery(id+"F8.opFillet","BLEND_EDGE",EDGE,{"blendedFrom":[makeQuery(id+"F1.opExtrude","CAP_EDGE",EDGE,{"disambiguationData":[OSD([subQ1])],"isStart":false}),makeQuery(id+"F1.opExtrude","CAP_FACE",FACE,{"disambiguationData":[OSD([sQuery(id+"F0.wireOp",EDGE,"E0.bottom"),sQuery(id+"F0.wireOp",EDGE,"E0.top"),subQ1,sQuery(id+"F0.wireOp",EDGE,"E0.right"),sQuery(id+"F0.wireOp",EDGE,"E5.bottom"),sQuery(id+"F0.wireOp",EDGE,"E5.top"),sQuery(id+"F0.wireOp",EDGE,"E5.left"),sQuery(id+"F0.wireOp",EDGE,"E5.right"),sQuery(id+"F0.wireOp",EDGE,"E6"),sQuery(id+"F0.wireOp",EDGE,"E7.MirrorC")])],"isStart":false})],"blendedInto":[makeQuery(id+"F1.opExtrude","CAP_FACE",FACE,{"disambiguationData":[OSD([sQuery(id+"F0.wireOp",EDGE,"E0.bottom"),sQuery(id+"F0.wireOp",EDGE,"E0.top"),subQ1,sQuery(id+"F0.wireOp",EDGE,"E0.right"),sQuery(id+"F0.wireOp",EDGE,"E5.bottom"),sQuery(id+"F0.wireOp",EDGE,"E5.top"),sQuery(id+"F0.wireOp",EDGE,"E5.left"),sQuery(id+"F0.wireOp",EDGE,"E5.right"),sQuery(id+"F0.wireOp",EDGE,"E6"),sQuery(id+"F0.wireOp",EDGE,"E7.MirrorC")])],"isStart":false})]});var subQ3=makeQuery(id+"F9.imprint","INTERSECT",VERTEX,{"disambiguationData":[OD(0.0)],"derivedFrom":[subQ2,subQ0]});Q8=makeQuery(id+"F9.imprint","IMPRINT",FACE,{"disambiguationData":[TD([[makeQuery(id+"F9.imprint","IMPRINT",EDGE,{"disambiguationData":[TD([[subQ3,-1.0]])],"derivedFrom":subQ0}),1.0]])]});}
            var Q9;
            {var subQ0=sQuery(id+"F9.wireOp",EDGE,"E11.2.4.0");var subQ1=sQuery(id+"F0.wireOp",EDGE,"E0.left");var subQ2=makeQuery(id+"F8.opFillet","BLEND_EDGE",EDGE,{"blendedFrom":[makeQuery(id+"F1.opExtrude","CAP_EDGE",EDGE,{"disambiguationData":[OSD([subQ1])],"isStart":false}),makeQuery(id+"F1.opExtrude","CAP_FACE",FACE,{"disambiguationData":[OSD([sQuery(id+"F0.wireOp",EDGE,"E0.bottom"),sQuery(id+"F0.wireOp",EDGE,"E0.top"),subQ1,sQuery(id+"F0.wireOp",EDGE,"E0.right"),sQuery(id+"F0.wireOp",EDGE,"E5.bottom"),sQuery(id+"F0.wireOp",EDGE,"E5.top"),sQuery(id+"F0.wireOp",EDGE,"E5.left"),sQuery(id+"F0.wireOp",EDGE,"E5.right"),sQuery(id+"F0.wireOp",EDGE,"E6"),sQuery(id+"F0.wireOp",EDGE,"E7.MirrorC")])],"isStart":false})],"blendedInto":[makeQuery(id+"F1.opExtrude","CAP_FACE",FACE,{"disambiguationData":[OSD([sQuery(id+"F0.wireOp",EDGE,"E0.bottom"),sQuery(id+"F0.wireOp",EDGE,"E0.top"),subQ1,sQuery(id+"F0.wireOp",EDGE,"E0.right"),sQuery(id+"F0.wireOp",EDGE,"E5.bottom"),sQuery(id+"F0.wireOp",EDGE,"E5.top"),sQuery(id+"F0.wireOp",EDGE,"E5.left"),sQuery(id+"F0.wireOp",EDGE,"E5.right"),sQuery(id+"F0.wireOp",EDGE,"E6"),sQuery(id+"F0.wireOp",EDGE,"E7.MirrorC")])],"isStart":false})]});var subQ3=makeQuery(id+"F9.imprint","INTERSECT",VERTEX,{"disambiguationData":[OD(0.0)],"derivedFrom":[subQ2,subQ0]});Q9=makeQuery(id+"F9.imprint","IMPRINT",FACE,{"disambiguationData":[TD([[makeQuery(id+"F9.imprint","IMPRINT",EDGE,{"disambiguationData":[TD([[subQ3,-1.0]])],"derivedFrom":subQ0}),1.0]])]});}
            var Q10;
            {var subQ0=sQuery(id+"F9.wireOp",EDGE,"E11.3.4.0");var subQ1=sQuery(id+"F0.wireOp",EDGE,"E0.left");var subQ2=makeQuery(id+"F8.opFillet","BLEND_EDGE",EDGE,{"blendedFrom":[makeQuery(id+"F1.opExtrude","CAP_EDGE",EDGE,{"disambiguationData":[OSD([subQ1])],"isStart":false}),makeQuery(id+"F1.opExtrude","CAP_FACE",FACE,{"disambiguationData":[OSD([sQuery(id+"F0.wireOp",EDGE,"E0.bottom"),sQuery(id+"F0.wireOp",EDGE,"E0.top"),subQ1,sQuery(id+"F0.wireOp",EDGE,"E0.right"),sQuery(id+"F0.wireOp",EDGE,"E5.bottom"),sQuery(id+"F0.wireOp",EDGE,"E5.top"),sQuery(id+"F0.wireOp",EDGE,"E5.left"),sQuery(id+"F0.wireOp",EDGE,"E5.right"),sQuery(id+"F0.wireOp",EDGE,"E6"),sQuery(id+"F0.wireOp",EDGE,"E7.MirrorC")])],"isStart":false})],"blendedInto":[makeQuery(id+"F1.opExtrude","CAP_FACE",FACE,{"disambiguationData":[OSD([sQuery(id+"F0.wireOp",EDGE,"E0.bottom"),sQuery(id+"F0.wireOp",EDGE,"E0.top"),subQ1,sQuery(id+"F0.wireOp",EDGE,"E0.right"),sQuery(id+"F0.wireOp",EDGE,"E5.bottom"),sQuery(id+"F0.wireOp",EDGE,"E5.top"),sQuery(id+"F0.wireOp",EDGE,"E5.left"),sQuery(id+"F0.wireOp",EDGE,"E5.right"),sQuery(id+"F0.wireOp",EDGE,"E6"),sQuery(id+"F0.wireOp",EDGE,"E7.MirrorC")])],"isStart":false})]});var subQ3=makeQuery(id+"F9.imprint","INTERSECT",VERTEX,{"disambiguationData":[OD(0.0)],"derivedFrom":[subQ2,subQ0]});Q10=makeQuery(id+"F9.imprint","IMPRINT",FACE,{"disambiguationData":[TD([[makeQuery(id+"F9.imprint","IMPRINT",EDGE,{"disambiguationData":[TD([[subQ3,-1.0]])],"derivedFrom":subQ0}),1.0]])]});}
            var Q11;
            {var subQ0=sQuery(id+"F9.wireOp",EDGE,"E11.4.4.0");var subQ1=sQuery(id+"F0.wireOp",EDGE,"E0.left");var subQ2=makeQuery(id+"F8.opFillet","BLEND_EDGE",EDGE,{"blendedFrom":[makeQuery(id+"F1.opExtrude","CAP_EDGE",EDGE,{"disambiguationData":[OSD([subQ1])],"isStart":false}),makeQuery(id+"F1.opExtrude","CAP_FACE",FACE,{"disambiguationData":[OSD([sQuery(id+"F0.wireOp",EDGE,"E0.bottom"),sQuery(id+"F0.wireOp",EDGE,"E0.top"),subQ1,sQuery(id+"F0.wireOp",EDGE,"E0.right"),sQuery(id+"F0.wireOp",EDGE,"E5.bottom"),sQuery(id+"F0.wireOp",EDGE,"E5.top"),sQuery(id+"F0.wireOp",EDGE,"E5.left"),sQuery(id+"F0.wireOp",EDGE,"E5.right"),sQuery(id+"F0.wireOp",EDGE,"E6"),sQuery(id+"F0.wireOp",EDGE,"E7.MirrorC")])],"isStart":false})],"blendedInto":[makeQuery(id+"F1.opExtrude","CAP_FACE",FACE,{"disambiguationData":[OSD([sQuery(id+"F0.wireOp",EDGE,"E0.bottom"),sQuery(id+"F0.wireOp",EDGE,"E0.top"),subQ1,sQuery(id+"F0.wireOp",EDGE,"E0.right"),sQuery(id+"F0.wireOp",EDGE,"E5.bottom"),sQuery(id+"F0.wireOp",EDGE,"E5.top"),sQuery(id+"F0.wireOp",EDGE,"E5.left"),sQuery(id+"F0.wireOp",EDGE,"E5.right"),sQuery(id+"F0.wireOp",EDGE,"E6"),sQuery(id+"F0.wireOp",EDGE,"E7.MirrorC")])],"isStart":false})]});var subQ3=makeQuery(id+"F9.imprint","INTERSECT",VERTEX,{"disambiguationData":[OD(0.0)],"derivedFrom":[subQ2,subQ0]});Q11=makeQuery(id+"F9.imprint","IMPRINT",FACE,{"disambiguationData":[TD([[makeQuery(id+"F9.imprint","IMPRINT",EDGE,{"disambiguationData":[TD([[subQ3,-1.0]])],"derivedFrom":subQ0}),1.0]])]});}
            var Q12;
            {var subQ0=sQuery(id+"F9.wireOp",EDGE,"E11.5.4.0");var subQ1=sQuery(id+"F0.wireOp",EDGE,"E0.left");var subQ2=makeQuery(id+"F8.opFillet","BLEND_EDGE",EDGE,{"blendedFrom":[makeQuery(id+"F1.opExtrude","CAP_EDGE",EDGE,{"disambiguationData":[OSD([subQ1])],"isStart":false}),makeQuery(id+"F1.opExtrude","CAP_FACE",FACE,{"disambiguationData":[OSD([sQuery(id+"F0.wireOp",EDGE,"E0.bottom"),sQuery(id+"F0.wireOp",EDGE,"E0.top"),subQ1,sQuery(id+"F0.wireOp",EDGE,"E0.right"),sQuery(id+"F0.wireOp",EDGE,"E5.bottom"),sQuery(id+"F0.wireOp",EDGE,"E5.top"),sQuery(id+"F0.wireOp",EDGE,"E5.left"),sQuery(id+"F0.wireOp",EDGE,"E5.right"),sQuery(id+"F0.wireOp",EDGE,"E6"),sQuery(id+"F0.wireOp",EDGE,"E7.MirrorC")])],"isStart":false})],"blendedInto":[makeQuery(id+"F1.opExtrude","CAP_FACE",FACE,{"disambiguationData":[OSD([sQuery(id+"F0.wireOp",EDGE,"E0.bottom"),sQuery(id+"F0.wireOp",EDGE,"E0.top"),subQ1,sQuery(id+"F0.wireOp",EDGE,"E0.right"),sQuery(id+"F0.wireOp",EDGE,"E5.bottom"),sQuery(id+"F0.wireOp",EDGE,"E5.top"),sQuery(id+"F0.wireOp",EDGE,"E5.left"),sQuery(id+"F0.wireOp",EDGE,"E5.right"),sQuery(id+"F0.wireOp",EDGE,"E6"),sQuery(id+"F0.wireOp",EDGE,"E7.MirrorC")])],"isStart":false})]});var subQ3=makeQuery(id+"F9.imprint","INTERSECT",VERTEX,{"disambiguationData":[OD(0.0)],"derivedFrom":[subQ2,subQ0]});Q12=makeQuery(id+"F9.imprint","IMPRINT",FACE,{"disambiguationData":[TD([[makeQuery(id+"F9.imprint","IMPRINT",EDGE,{"disambiguationData":[TD([[subQ3,-1.0]])],"derivedFrom":subQ0}),1.0]])]});}
            var Q13;
            {var subQ0=sQuery(id+"F9.wireOp",EDGE,"E11.6.4.0");var subQ1=sQuery(id+"F0.wireOp",EDGE,"E0.left");var subQ2=makeQuery(id+"F8.opFillet","BLEND_EDGE",EDGE,{"blendedFrom":[makeQuery(id+"F1.opExtrude","CAP_EDGE",EDGE,{"disambiguationData":[OSD([subQ1])],"isStart":false}),makeQuery(id+"F1.opExtrude","CAP_FACE",FACE,{"disambiguationData":[OSD([sQuery(id+"F0.wireOp",EDGE,"E0.bottom"),sQuery(id+"F0.wireOp",EDGE,"E0.top"),subQ1,sQuery(id+"F0.wireOp",EDGE,"E0.right"),sQuery(id+"F0.wireOp",EDGE,"E5.bottom"),sQuery(id+"F0.wireOp",EDGE,"E5.top"),sQuery(id+"F0.wireOp",EDGE,"E5.left"),sQuery(id+"F0.wireOp",EDGE,"E5.right"),sQuery(id+"F0.wireOp",EDGE,"E6"),sQuery(id+"F0.wireOp",EDGE,"E7.MirrorC")])],"isStart":false})],"blendedInto":[makeQuery(id+"F1.opExtrude","CAP_FACE",FACE,{"disambiguationData":[OSD([sQuery(id+"F0.wireOp",EDGE,"E0.bottom"),sQuery(id+"F0.wireOp",EDGE,"E0.top"),subQ1,sQuery(id+"F0.wireOp",EDGE,"E0.right"),sQuery(id+"F0.wireOp",EDGE,"E5.bottom"),sQuery(id+"F0.wireOp",EDGE,"E5.top"),sQuery(id+"F0.wireOp",EDGE,"E5.left"),sQuery(id+"F0.wireOp",EDGE,"E5.right"),sQuery(id+"F0.wireOp",EDGE,"E6"),sQuery(id+"F0.wireOp",EDGE,"E7.MirrorC")])],"isStart":false})]});var subQ3=makeQuery(id+"F9.imprint","INTERSECT",VERTEX,{"disambiguationData":[OD(0.0)],"derivedFrom":[subQ2,subQ0]});Q13=makeQuery(id+"F9.imprint","IMPRINT",FACE,{"disambiguationData":[TD([[makeQuery(id+"F9.imprint","IMPRINT",EDGE,{"disambiguationData":[TD([[subQ3,-1.0]])],"derivedFrom":subQ0}),1.0]])]});}
            var Q14;
            {var subQ0=sQuery(id+"F9.wireOp",EDGE,"E11.7.4.0");var subQ1=sQuery(id+"F0.wireOp",EDGE,"E0.left");var subQ2=makeQuery(id+"F8.opFillet","BLEND_EDGE",EDGE,{"blendedFrom":[makeQuery(id+"F1.opExtrude","CAP_EDGE",EDGE,{"disambiguationData":[OSD([subQ1])],"isStart":false}),makeQuery(id+"F1.opExtrude","CAP_FACE",FACE,{"disambiguationData":[OSD([sQuery(id+"F0.wireOp",EDGE,"E0.bottom"),sQuery(id+"F0.wireOp",EDGE,"E0.top"),subQ1,sQuery(id+"F0.wireOp",EDGE,"E0.right"),sQuery(id+"F0.wireOp",EDGE,"E5.bottom"),sQuery(id+"F0.wireOp",EDGE,"E5.top"),sQuery(id+"F0.wireOp",EDGE,"E5.left"),sQuery(id+"F0.wireOp",EDGE,"E5.right"),sQuery(id+"F0.wireOp",EDGE,"E6"),sQuery(id+"F0.wireOp",EDGE,"E7.MirrorC")])],"isStart":false})],"blendedInto":[makeQuery(id+"F1.opExtrude","CAP_FACE",FACE,{"disambiguationData":[OSD([sQuery(id+"F0.wireOp",EDGE,"E0.bottom"),sQuery(id+"F0.wireOp",EDGE,"E0.top"),subQ1,sQuery(id+"F0.wireOp",EDGE,"E0.right"),sQuery(id+"F0.wireOp",EDGE,"E5.bottom"),sQuery(id+"F0.wireOp",EDGE,"E5.top"),sQuery(id+"F0.wireOp",EDGE,"E5.left"),sQuery(id+"F0.wireOp",EDGE,"E5.right"),sQuery(id+"F0.wireOp",EDGE,"E6"),sQuery(id+"F0.wireOp",EDGE,"E7.MirrorC")])],"isStart":false})]});var subQ3=makeQuery(id+"F9.imprint","INTERSECT",VERTEX,{"disambiguationData":[OD(0.0)],"derivedFrom":[subQ2,subQ0]});Q14=makeQuery(id+"F9.imprint","IMPRINT",FACE,{"disambiguationData":[TD([[makeQuery(id+"F9.imprint","IMPRINT",EDGE,{"disambiguationData":[TD([[subQ3,-1.0]])],"derivedFrom":subQ0}),1.0]])]});}
            var Q15;
            Q15=makeQuery(id+"F9.imprint","IMPRINT",FACE,{"disambiguationData":[TD([[makeQuery(id+"F9.imprint","IMPRINT",EDGE,{"derivedFrom":sQuery(id+"F9.wireOp",EDGE,"E11.7.3.0")}),1.0]])]});
            var Q16;
            Q16=makeQuery(id+"F9.imprint","IMPRINT",FACE,{"disambiguationData":[TD([[makeQuery(id+"F9.imprint","IMPRINT",EDGE,{"derivedFrom":sQuery(id+"F9.wireOp",EDGE,"E11.7.2.0")}),1.0]])]});
            var Q17;
            Q17=makeQuery(id+"F9.imprint","IMPRINT",FACE,{"disambiguationData":[TD([[makeQuery(id+"F9.imprint","IMPRINT",EDGE,{"derivedFrom":sQuery(id+"F9.wireOp",EDGE,"E11.7.1.0")}),1.0]])]});
            var Q18;
            Q18=makeQuery(id+"F9.imprint","IMPRINT",FACE,{"disambiguationData":[TD([[makeQuery(id+"F9.imprint","IMPRINT",EDGE,{"derivedFrom":sQuery(id+"F9.wireOp",EDGE,"E11.7.0.0")}),1.0]])]});
            var Q19;
            Q19=makeQuery(id+"F9.imprint","IMPRINT",FACE,{"disambiguationData":[TD([[makeQuery(id+"F9.imprint","IMPRINT",EDGE,{"derivedFrom":sQuery(id+"F9.wireOp",EDGE,"E13.1.7.0")}),1.0]])]});
            var Q20;
            Q20=makeQuery(id+"F9.imprint","IMPRINT",FACE,{"disambiguationData":[TD([[makeQuery(id+"F9.imprint","IMPRINT",EDGE,{"derivedFrom":sQuery(id+"F9.wireOp",EDGE,"E13.2.7.0")}),1.0]])]});
            var Q21;
            Q21=makeQuery(id+"F9.imprint","IMPRINT",FACE,{"disambiguationData":[TD([[makeQuery(id+"F9.imprint","IMPRINT",EDGE,{"derivedFrom":sQuery(id+"F9.wireOp",EDGE,"E13.3.7.0")}),1.0]])]});
            var Q22;
            {var subQ0=sQuery(id+"F9.wireOp",EDGE,"E13.4.7.0");var subQ1=sQuery(id+"F0.wireOp",EDGE,"E0.right");var subQ2=makeQuery(id+"F8.opFillet","BLEND_EDGE",EDGE,{"blendedFrom":[makeQuery(id+"F1.opExtrude","CAP_EDGE",EDGE,{"disambiguationData":[OSD([subQ1])],"isStart":false}),makeQuery(id+"F1.opExtrude","CAP_FACE",FACE,{"disambiguationData":[OSD([sQuery(id+"F0.wireOp",EDGE,"E0.bottom"),sQuery(id+"F0.wireOp",EDGE,"E0.top"),sQuery(id+"F0.wireOp",EDGE,"E0.left"),subQ1,sQuery(id+"F0.wireOp",EDGE,"E5.bottom"),sQuery(id+"F0.wireOp",EDGE,"E5.top"),sQuery(id+"F0.wireOp",EDGE,"E5.left"),sQuery(id+"F0.wireOp",EDGE,"E5.right"),sQuery(id+"F0.wireOp",EDGE,"E6"),sQuery(id+"F0.wireOp",EDGE,"E7.MirrorC")])],"isStart":false})],"blendedInto":[makeQuery(id+"F1.opExtrude","CAP_FACE",FACE,{"disambiguationData":[OSD([sQuery(id+"F0.wireOp",EDGE,"E0.bottom"),sQuery(id+"F0.wireOp",EDGE,"E0.top"),sQuery(id+"F0.wireOp",EDGE,"E0.left"),subQ1,sQuery(id+"F0.wireOp",EDGE,"E5.bottom"),sQuery(id+"F0.wireOp",EDGE,"E5.top"),sQuery(id+"F0.wireOp",EDGE,"E5.left"),sQuery(id+"F0.wireOp",EDGE,"E5.right"),sQuery(id+"F0.wireOp",EDGE,"E6"),sQuery(id+"F0.wireOp",EDGE,"E7.MirrorC")])],"isStart":false})]});var subQ3=makeQuery(id+"F9.imprint","INTERSECT",VERTEX,{"disambiguationData":[OD(0.0)],"derivedFrom":[subQ2,subQ0]});Q22=makeQuery(id+"F9.imprint","IMPRINT",FACE,{"disambiguationData":[TD([[makeQuery(id+"F9.imprint","IMPRINT",EDGE,{"disambiguationData":[TD([[subQ3,1.0]])],"derivedFrom":subQ0}),1.0]])]});}
            var Q23;
            {var subQ0=sQuery(id+"F9.wireOp",EDGE,"E13.4.6.0");var subQ1=sQuery(id+"F0.wireOp",EDGE,"E0.right");var subQ2=makeQuery(id+"F8.opFillet","BLEND_EDGE",EDGE,{"blendedFrom":[makeQuery(id+"F1.opExtrude","CAP_EDGE",EDGE,{"disambiguationData":[OSD([subQ1])],"isStart":false}),makeQuery(id+"F1.opExtrude","CAP_FACE",FACE,{"disambiguationData":[OSD([sQuery(id+"F0.wireOp",EDGE,"E0.bottom"),sQuery(id+"F0.wireOp",EDGE,"E0.top"),sQuery(id+"F0.wireOp",EDGE,"E0.left"),subQ1,sQuery(id+"F0.wireOp",EDGE,"E5.bottom"),sQuery(id+"F0.wireOp",EDGE,"E5.top"),sQuery(id+"F0.wireOp",EDGE,"E5.left"),sQuery(id+"F0.wireOp",EDGE,"E5.right"),sQuery(id+"F0.wireOp",EDGE,"E6"),sQuery(id+"F0.wireOp",EDGE,"E7.MirrorC")])],"isStart":false})],"blendedInto":[makeQuery(id+"F1.opExtrude","CAP_FACE",FACE,{"disambiguationData":[OSD([sQuery(id+"F0.wireOp",EDGE,"E0.bottom"),sQuery(id+"F0.wireOp",EDGE,"E0.top"),sQuery(id+"F0.wireOp",EDGE,"E0.left"),subQ1,sQuery(id+"F0.wireOp",EDGE,"E5.bottom"),sQuery(id+"F0.wireOp",EDGE,"E5.top"),sQuery(id+"F0.wireOp",EDGE,"E5.left"),sQuery(id+"F0.wireOp",EDGE,"E5.right"),sQuery(id+"F0.wireOp",EDGE,"E6"),sQuery(id+"F0.wireOp",EDGE,"E7.MirrorC")])],"isStart":false})]});var subQ3=makeQuery(id+"F9.imprint","INTERSECT",VERTEX,{"disambiguationData":[OD(0.0)],"derivedFrom":[subQ2,subQ0]});Q23=makeQuery(id+"F9.imprint","IMPRINT",FACE,{"disambiguationData":[TD([[makeQuery(id+"F9.imprint","IMPRINT",EDGE,{"disambiguationData":[TD([[subQ3,1.0]])],"derivedFrom":subQ0}),1.0]])]});}
            var Q24;
            {var subQ0=sQuery(id+"F9.wireOp",EDGE,"E13.4.5.0");var subQ1=sQuery(id+"F0.wireOp",EDGE,"E0.right");var subQ2=makeQuery(id+"F8.opFillet","BLEND_EDGE",EDGE,{"blendedFrom":[makeQuery(id+"F1.opExtrude","CAP_EDGE",EDGE,{"disambiguationData":[OSD([subQ1])],"isStart":false}),makeQuery(id+"F1.opExtrude","CAP_FACE",FACE,{"disambiguationData":[OSD([sQuery(id+"F0.wireOp",EDGE,"E0.bottom"),sQuery(id+"F0.wireOp",EDGE,"E0.top"),sQuery(id+"F0.wireOp",EDGE,"E0.left"),subQ1,sQuery(id+"F0.wireOp",EDGE,"E5.bottom"),sQuery(id+"F0.wireOp",EDGE,"E5.top"),sQuery(id+"F0.wireOp",EDGE,"E5.left"),sQuery(id+"F0.wireOp",EDGE,"E5.right"),sQuery(id+"F0.wireOp",EDGE,"E6"),sQuery(id+"F0.wireOp",EDGE,"E7.MirrorC")])],"isStart":false})],"blendedInto":[makeQuery(id+"F1.opExtrude","CAP_FACE",FACE,{"disambiguationData":[OSD([sQuery(id+"F0.wireOp",EDGE,"E0.bottom"),sQuery(id+"F0.wireOp",EDGE,"E0.top"),sQuery(id+"F0.wireOp",EDGE,"E0.left"),subQ1,sQuery(id+"F0.wireOp",EDGE,"E5.bottom"),sQuery(id+"F0.wireOp",EDGE,"E5.top"),sQuery(id+"F0.wireOp",EDGE,"E5.left"),sQuery(id+"F0.wireOp",EDGE,"E5.right"),sQuery(id+"F0.wireOp",EDGE,"E6"),sQuery(id+"F0.wireOp",EDGE,"E7.MirrorC")])],"isStart":false})]});var subQ3=makeQuery(id+"F9.imprint","INTERSECT",VERTEX,{"disambiguationData":[OD(0.0)],"derivedFrom":[subQ2,subQ0]});Q24=makeQuery(id+"F9.imprint","IMPRINT",FACE,{"disambiguationData":[TD([[makeQuery(id+"F9.imprint","IMPRINT",EDGE,{"disambiguationData":[TD([[subQ3,1.0]])],"derivedFrom":subQ0}),1.0]])]});}
            var Q25;
            {var subQ0=sQuery(id+"F9.wireOp",EDGE,"E13.4.4.0");var subQ1=sQuery(id+"F0.wireOp",EDGE,"E0.right");var subQ2=makeQuery(id+"F8.opFillet","BLEND_EDGE",EDGE,{"blendedFrom":[makeQuery(id+"F1.opExtrude","CAP_EDGE",EDGE,{"disambiguationData":[OSD([subQ1])],"isStart":false}),makeQuery(id+"F1.opExtrude","CAP_FACE",FACE,{"disambiguationData":[OSD([sQuery(id+"F0.wireOp",EDGE,"E0.bottom"),sQuery(id+"F0.wireOp",EDGE,"E0.top"),sQuery(id+"F0.wireOp",EDGE,"E0.left"),subQ1,sQuery(id+"F0.wireOp",EDGE,"E5.bottom"),sQuery(id+"F0.wireOp",EDGE,"E5.top"),sQuery(id+"F0.wireOp",EDGE,"E5.left"),sQuery(id+"F0.wireOp",EDGE,"E5.right"),sQuery(id+"F0.wireOp",EDGE,"E6"),sQuery(id+"F0.wireOp",EDGE,"E7.MirrorC")])],"isStart":false})],"blendedInto":[makeQuery(id+"F1.opExtrude","CAP_FACE",FACE,{"disambiguationData":[OSD([sQuery(id+"F0.wireOp",EDGE,"E0.bottom"),sQuery(id+"F0.wireOp",EDGE,"E0.top"),sQuery(id+"F0.wireOp",EDGE,"E0.left"),subQ1,sQuery(id+"F0.wireOp",EDGE,"E5.bottom"),sQuery(id+"F0.wireOp",EDGE,"E5.top"),sQuery(id+"F0.wireOp",EDGE,"E5.left"),sQuery(id+"F0.wireOp",EDGE,"E5.right"),sQuery(id+"F0.wireOp",EDGE,"E6"),sQuery(id+"F0.wireOp",EDGE,"E7.MirrorC")])],"isStart":false})]});var subQ3=makeQuery(id+"F9.imprint","INTERSECT",VERTEX,{"disambiguationData":[OD(0.0)],"derivedFrom":[subQ2,subQ0]});Q25=makeQuery(id+"F9.imprint","IMPRINT",FACE,{"disambiguationData":[TD([[makeQuery(id+"F9.imprint","IMPRINT",EDGE,{"disambiguationData":[TD([[subQ3,1.0]])],"derivedFrom":subQ0}),1.0]])]});}
            var Q26;
            {var subQ0=sQuery(id+"F9.wireOp",EDGE,"E13.4.3.0");var subQ1=sQuery(id+"F0.wireOp",EDGE,"E0.right");var subQ2=makeQuery(id+"F8.opFillet","BLEND_EDGE",EDGE,{"blendedFrom":[makeQuery(id+"F1.opExtrude","CAP_EDGE",EDGE,{"disambiguationData":[OSD([subQ1])],"isStart":false}),makeQuery(id+"F1.opExtrude","CAP_FACE",FACE,{"disambiguationData":[OSD([sQuery(id+"F0.wireOp",EDGE,"E0.bottom"),sQuery(id+"F0.wireOp",EDGE,"E0.top"),sQuery(id+"F0.wireOp",EDGE,"E0.left"),subQ1,sQuery(id+"F0.wireOp",EDGE,"E5.bottom"),sQuery(id+"F0.wireOp",EDGE,"E5.top"),sQuery(id+"F0.wireOp",EDGE,"E5.left"),sQuery(id+"F0.wireOp",EDGE,"E5.right"),sQuery(id+"F0.wireOp",EDGE,"E6"),sQuery(id+"F0.wireOp",EDGE,"E7.MirrorC")])],"isStart":false})],"blendedInto":[makeQuery(id+"F1.opExtrude","CAP_FACE",FACE,{"disambiguationData":[OSD([sQuery(id+"F0.wireOp",EDGE,"E0.bottom"),sQuery(id+"F0.wireOp",EDGE,"E0.top"),sQuery(id+"F0.wireOp",EDGE,"E0.left"),subQ1,sQuery(id+"F0.wireOp",EDGE,"E5.bottom"),sQuery(id+"F0.wireOp",EDGE,"E5.top"),sQuery(id+"F0.wireOp",EDGE,"E5.left"),sQuery(id+"F0.wireOp",EDGE,"E5.right"),sQuery(id+"F0.wireOp",EDGE,"E6"),sQuery(id+"F0.wireOp",EDGE,"E7.MirrorC")])],"isStart":false})]});var subQ3=makeQuery(id+"F9.imprint","INTERSECT",VERTEX,{"disambiguationData":[OD(0.0)],"derivedFrom":[subQ2,subQ0]});Q26=makeQuery(id+"F9.imprint","IMPRINT",FACE,{"disambiguationData":[TD([[makeQuery(id+"F9.imprint","IMPRINT",EDGE,{"disambiguationData":[TD([[subQ3,1.0]])],"derivedFrom":subQ0}),1.0]])]});}
            var Q27;
            {var subQ0=sQuery(id+"F9.wireOp",EDGE,"E13.4.2.0");var subQ1=sQuery(id+"F0.wireOp",EDGE,"E0.right");var subQ2=makeQuery(id+"F8.opFillet","BLEND_EDGE",EDGE,{"blendedFrom":[makeQuery(id+"F1.opExtrude","CAP_EDGE",EDGE,{"disambiguationData":[OSD([subQ1])],"isStart":false}),makeQuery(id+"F1.opExtrude","CAP_FACE",FACE,{"disambiguationData":[OSD([sQuery(id+"F0.wireOp",EDGE,"E0.bottom"),sQuery(id+"F0.wireOp",EDGE,"E0.top"),sQuery(id+"F0.wireOp",EDGE,"E0.left"),subQ1,sQuery(id+"F0.wireOp",EDGE,"E5.bottom"),sQuery(id+"F0.wireOp",EDGE,"E5.top"),sQuery(id+"F0.wireOp",EDGE,"E5.left"),sQuery(id+"F0.wireOp",EDGE,"E5.right"),sQuery(id+"F0.wireOp",EDGE,"E6"),sQuery(id+"F0.wireOp",EDGE,"E7.MirrorC")])],"isStart":false})],"blendedInto":[makeQuery(id+"F1.opExtrude","CAP_FACE",FACE,{"disambiguationData":[OSD([sQuery(id+"F0.wireOp",EDGE,"E0.bottom"),sQuery(id+"F0.wireOp",EDGE,"E0.top"),sQuery(id+"F0.wireOp",EDGE,"E0.left"),subQ1,sQuery(id+"F0.wireOp",EDGE,"E5.bottom"),sQuery(id+"F0.wireOp",EDGE,"E5.top"),sQuery(id+"F0.wireOp",EDGE,"E5.left"),sQuery(id+"F0.wireOp",EDGE,"E5.right"),sQuery(id+"F0.wireOp",EDGE,"E6"),sQuery(id+"F0.wireOp",EDGE,"E7.MirrorC")])],"isStart":false})]});var subQ3=makeQuery(id+"F9.imprint","INTERSECT",VERTEX,{"disambiguationData":[OD(0.0)],"derivedFrom":[subQ2,subQ0]});Q27=makeQuery(id+"F9.imprint","IMPRINT",FACE,{"disambiguationData":[TD([[makeQuery(id+"F9.imprint","IMPRINT",EDGE,{"disambiguationData":[TD([[subQ3,1.0]])],"derivedFrom":subQ0}),1.0]])]});}
            var Q28;
            {var subQ0=sQuery(id+"F9.wireOp",EDGE,"E13.4.1.0");var subQ1=sQuery(id+"F0.wireOp",EDGE,"E0.right");var subQ2=makeQuery(id+"F8.opFillet","BLEND_EDGE",EDGE,{"blendedFrom":[makeQuery(id+"F1.opExtrude","CAP_EDGE",EDGE,{"disambiguationData":[OSD([subQ1])],"isStart":false}),makeQuery(id+"F1.opExtrude","CAP_FACE",FACE,{"disambiguationData":[OSD([sQuery(id+"F0.wireOp",EDGE,"E0.bottom"),sQuery(id+"F0.wireOp",EDGE,"E0.top"),sQuery(id+"F0.wireOp",EDGE,"E0.left"),subQ1,sQuery(id+"F0.wireOp",EDGE,"E5.bottom"),sQuery(id+"F0.wireOp",EDGE,"E5.top"),sQuery(id+"F0.wireOp",EDGE,"E5.left"),sQuery(id+"F0.wireOp",EDGE,"E5.right"),sQuery(id+"F0.wireOp",EDGE,"E6"),sQuery(id+"F0.wireOp",EDGE,"E7.MirrorC")])],"isStart":false})],"blendedInto":[makeQuery(id+"F1.opExtrude","CAP_FACE",FACE,{"disambiguationData":[OSD([sQuery(id+"F0.wireOp",EDGE,"E0.bottom"),sQuery(id+"F0.wireOp",EDGE,"E0.top"),sQuery(id+"F0.wireOp",EDGE,"E0.left"),subQ1,sQuery(id+"F0.wireOp",EDGE,"E5.bottom"),sQuery(id+"F0.wireOp",EDGE,"E5.top"),sQuery(id+"F0.wireOp",EDGE,"E5.left"),sQuery(id+"F0.wireOp",EDGE,"E5.right"),sQuery(id+"F0.wireOp",EDGE,"E6"),sQuery(id+"F0.wireOp",EDGE,"E7.MirrorC")])],"isStart":false})]});var subQ3=makeQuery(id+"F9.imprint","INTERSECT",VERTEX,{"disambiguationData":[OD(0.0)],"derivedFrom":[subQ2,subQ0]});Q28=makeQuery(id+"F9.imprint","IMPRINT",FACE,{"disambiguationData":[TD([[makeQuery(id+"F9.imprint","IMPRINT",EDGE,{"disambiguationData":[TD([[subQ3,1.0]])],"derivedFrom":subQ0}),1.0]])]});}
            var Q29;
            {var subQ0=sQuery(id+"F9.wireOp",EDGE,"E10.4.0.0");var subQ1=sQuery(id+"F0.wireOp",EDGE,"E0.right");var subQ2=makeQuery(id+"F8.opFillet","BLEND_EDGE",EDGE,{"blendedFrom":[makeQuery(id+"F1.opExtrude","CAP_EDGE",EDGE,{"disambiguationData":[OSD([subQ1])],"isStart":false}),makeQuery(id+"F1.opExtrude","CAP_FACE",FACE,{"disambiguationData":[OSD([sQuery(id+"F0.wireOp",EDGE,"E0.bottom"),sQuery(id+"F0.wireOp",EDGE,"E0.top"),sQuery(id+"F0.wireOp",EDGE,"E0.left"),subQ1,sQuery(id+"F0.wireOp",EDGE,"E5.bottom"),sQuery(id+"F0.wireOp",EDGE,"E5.top"),sQuery(id+"F0.wireOp",EDGE,"E5.left"),sQuery(id+"F0.wireOp",EDGE,"E5.right"),sQuery(id+"F0.wireOp",EDGE,"E6"),sQuery(id+"F0.wireOp",EDGE,"E7.MirrorC")])],"isStart":false})],"blendedInto":[makeQuery(id+"F1.opExtrude","CAP_FACE",FACE,{"disambiguationData":[OSD([sQuery(id+"F0.wireOp",EDGE,"E0.bottom"),sQuery(id+"F0.wireOp",EDGE,"E0.top"),sQuery(id+"F0.wireOp",EDGE,"E0.left"),subQ1,sQuery(id+"F0.wireOp",EDGE,"E5.bottom"),sQuery(id+"F0.wireOp",EDGE,"E5.top"),sQuery(id+"F0.wireOp",EDGE,"E5.left"),sQuery(id+"F0.wireOp",EDGE,"E5.right"),sQuery(id+"F0.wireOp",EDGE,"E6"),sQuery(id+"F0.wireOp",EDGE,"E7.MirrorC")])],"isStart":false})]});var subQ3=makeQuery(id+"F9.imprint","INTERSECT",VERTEX,{"disambiguationData":[OD(0.0)],"derivedFrom":[subQ2,subQ0]});Q29=makeQuery(id+"F9.imprint","IMPRINT",FACE,{"disambiguationData":[TD([[makeQuery(id+"F9.imprint","IMPRINT",EDGE,{"disambiguationData":[TD([[subQ3,-1.0]])],"derivedFrom":subQ0}),1.0]])]});}
            var Q30;
            {var subQ0=sQuery(id+"F9.wireOp",EDGE,"E10.4.1.0");var subQ1=sQuery(id+"F0.wireOp",EDGE,"E0.right");var subQ2=makeQuery(id+"F8.opFillet","BLEND_EDGE",EDGE,{"blendedFrom":[makeQuery(id+"F1.opExtrude","CAP_EDGE",EDGE,{"disambiguationData":[OSD([subQ1])],"isStart":false}),makeQuery(id+"F1.opExtrude","CAP_FACE",FACE,{"disambiguationData":[OSD([sQuery(id+"F0.wireOp",EDGE,"E0.bottom"),sQuery(id+"F0.wireOp",EDGE,"E0.top"),sQuery(id+"F0.wireOp",EDGE,"E0.left"),subQ1,sQuery(id+"F0.wireOp",EDGE,"E5.bottom"),sQuery(id+"F0.wireOp",EDGE,"E5.top"),sQuery(id+"F0.wireOp",EDGE,"E5.left"),sQuery(id+"F0.wireOp",EDGE,"E5.right"),sQuery(id+"F0.wireOp",EDGE,"E6"),sQuery(id+"F0.wireOp",EDGE,"E7.MirrorC")])],"isStart":false})],"blendedInto":[makeQuery(id+"F1.opExtrude","CAP_FACE",FACE,{"disambiguationData":[OSD([sQuery(id+"F0.wireOp",EDGE,"E0.bottom"),sQuery(id+"F0.wireOp",EDGE,"E0.top"),sQuery(id+"F0.wireOp",EDGE,"E0.left"),subQ1,sQuery(id+"F0.wireOp",EDGE,"E5.bottom"),sQuery(id+"F0.wireOp",EDGE,"E5.top"),sQuery(id+"F0.wireOp",EDGE,"E5.left"),sQuery(id+"F0.wireOp",EDGE,"E5.right"),sQuery(id+"F0.wireOp",EDGE,"E6"),sQuery(id+"F0.wireOp",EDGE,"E7.MirrorC")])],"isStart":false})]});var subQ3=makeQuery(id+"F9.imprint","INTERSECT",VERTEX,{"disambiguationData":[OD(0.0)],"derivedFrom":[subQ2,subQ0]});Q30=makeQuery(id+"F9.imprint","IMPRINT",FACE,{"disambiguationData":[TD([[makeQuery(id+"F9.imprint","IMPRINT",EDGE,{"disambiguationData":[TD([[subQ3,-1.0]])],"derivedFrom":subQ0}),1.0]])]});}
            var Q31;
            {var subQ0=sQuery(id+"F9.wireOp",EDGE,"E10.4.2.0");var subQ1=sQuery(id+"F0.wireOp",EDGE,"E0.right");var subQ2=makeQuery(id+"F8.opFillet","BLEND_EDGE",EDGE,{"blendedFrom":[makeQuery(id+"F1.opExtrude","CAP_EDGE",EDGE,{"disambiguationData":[OSD([subQ1])],"isStart":false}),makeQuery(id+"F1.opExtrude","CAP_FACE",FACE,{"disambiguationData":[OSD([sQuery(id+"F0.wireOp",EDGE,"E0.bottom"),sQuery(id+"F0.wireOp",EDGE,"E0.top"),sQuery(id+"F0.wireOp",EDGE,"E0.left"),subQ1,sQuery(id+"F0.wireOp",EDGE,"E5.bottom"),sQuery(id+"F0.wireOp",EDGE,"E5.top"),sQuery(id+"F0.wireOp",EDGE,"E5.left"),sQuery(id+"F0.wireOp",EDGE,"E5.right"),sQuery(id+"F0.wireOp",EDGE,"E6"),sQuery(id+"F0.wireOp",EDGE,"E7.MirrorC")])],"isStart":false})],"blendedInto":[makeQuery(id+"F1.opExtrude","CAP_FACE",FACE,{"disambiguationData":[OSD([sQuery(id+"F0.wireOp",EDGE,"E0.bottom"),sQuery(id+"F0.wireOp",EDGE,"E0.top"),sQuery(id+"F0.wireOp",EDGE,"E0.left"),subQ1,sQuery(id+"F0.wireOp",EDGE,"E5.bottom"),sQuery(id+"F0.wireOp",EDGE,"E5.top"),sQuery(id+"F0.wireOp",EDGE,"E5.left"),sQuery(id+"F0.wireOp",EDGE,"E5.right"),sQuery(id+"F0.wireOp",EDGE,"E6"),sQuery(id+"F0.wireOp",EDGE,"E7.MirrorC")])],"isStart":false})]});var subQ3=makeQuery(id+"F9.imprint","INTERSECT",VERTEX,{"disambiguationData":[OD(0.0)],"derivedFrom":[subQ2,subQ0]});Q31=makeQuery(id+"F9.imprint","IMPRINT",FACE,{"disambiguationData":[TD([[makeQuery(id+"F9.imprint","IMPRINT",EDGE,{"disambiguationData":[TD([[subQ3,-1.0]])],"derivedFrom":subQ0}),1.0]])]});}
            var Q32;
            {var subQ0=sQuery(id+"F9.wireOp",EDGE,"E10.4.3.0");var subQ1=sQuery(id+"F0.wireOp",EDGE,"E0.right");var subQ2=makeQuery(id+"F8.opFillet","BLEND_EDGE",EDGE,{"blendedFrom":[makeQuery(id+"F1.opExtrude","CAP_EDGE",EDGE,{"disambiguationData":[OSD([subQ1])],"isStart":false}),makeQuery(id+"F1.opExtrude","CAP_FACE",FACE,{"disambiguationData":[OSD([sQuery(id+"F0.wireOp",EDGE,"E0.bottom"),sQuery(id+"F0.wireOp",EDGE,"E0.top"),sQuery(id+"F0.wireOp",EDGE,"E0.left"),subQ1,sQuery(id+"F0.wireOp",EDGE,"E5.bottom"),sQuery(id+"F0.wireOp",EDGE,"E5.top"),sQuery(id+"F0.wireOp",EDGE,"E5.left"),sQuery(id+"F0.wireOp",EDGE,"E5.right"),sQuery(id+"F0.wireOp",EDGE,"E6"),sQuery(id+"F0.wireOp",EDGE,"E7.MirrorC")])],"isStart":false})],"blendedInto":[makeQuery(id+"F1.opExtrude","CAP_FACE",FACE,{"disambiguationData":[OSD([sQuery(id+"F0.wireOp",EDGE,"E0.bottom"),sQuery(id+"F0.wireOp",EDGE,"E0.top"),sQuery(id+"F0.wireOp",EDGE,"E0.left"),subQ1,sQuery(id+"F0.wireOp",EDGE,"E5.bottom"),sQuery(id+"F0.wireOp",EDGE,"E5.top"),sQuery(id+"F0.wireOp",EDGE,"E5.left"),sQuery(id+"F0.wireOp",EDGE,"E5.right"),sQuery(id+"F0.wireOp",EDGE,"E6"),sQuery(id+"F0.wireOp",EDGE,"E7.MirrorC")])],"isStart":false})]});var subQ3=makeQuery(id+"F9.imprint","INTERSECT",VERTEX,{"disambiguationData":[OD(0.0)],"derivedFrom":[subQ2,subQ0]});Q32=makeQuery(id+"F9.imprint","IMPRINT",FACE,{"disambiguationData":[TD([[makeQuery(id+"F9.imprint","IMPRINT",EDGE,{"disambiguationData":[TD([[subQ3,-1.0]])],"derivedFrom":subQ0}),1.0]])]});}
            var Q33;
            {var subQ0=sQuery(id+"F9.wireOp",EDGE,"E10.4.4.0");var subQ1=sQuery(id+"F0.wireOp",EDGE,"E0.right");var subQ2=makeQuery(id+"F8.opFillet","BLEND_EDGE",EDGE,{"blendedFrom":[makeQuery(id+"F1.opExtrude","CAP_EDGE",EDGE,{"disambiguationData":[OSD([subQ1])],"isStart":false}),makeQuery(id+"F1.opExtrude","CAP_FACE",FACE,{"disambiguationData":[OSD([sQuery(id+"F0.wireOp",EDGE,"E0.bottom"),sQuery(id+"F0.wireOp",EDGE,"E0.top"),sQuery(id+"F0.wireOp",EDGE,"E0.left"),subQ1,sQuery(id+"F0.wireOp",EDGE,"E5.bottom"),sQuery(id+"F0.wireOp",EDGE,"E5.top"),sQuery(id+"F0.wireOp",EDGE,"E5.left"),sQuery(id+"F0.wireOp",EDGE,"E5.right"),sQuery(id+"F0.wireOp",EDGE,"E6"),sQuery(id+"F0.wireOp",EDGE,"E7.MirrorC")])],"isStart":false})],"blendedInto":[makeQuery(id+"F1.opExtrude","CAP_FACE",FACE,{"disambiguationData":[OSD([sQuery(id+"F0.wireOp",EDGE,"E0.bottom"),sQuery(id+"F0.wireOp",EDGE,"E0.top"),sQuery(id+"F0.wireOp",EDGE,"E0.left"),subQ1,sQuery(id+"F0.wireOp",EDGE,"E5.bottom"),sQuery(id+"F0.wireOp",EDGE,"E5.top"),sQuery(id+"F0.wireOp",EDGE,"E5.left"),sQuery(id+"F0.wireOp",EDGE,"E5.right"),sQuery(id+"F0.wireOp",EDGE,"E6"),sQuery(id+"F0.wireOp",EDGE,"E7.MirrorC")])],"isStart":false})]});var subQ3=makeQuery(id+"F9.imprint","INTERSECT",VERTEX,{"disambiguationData":[OD(0.0)],"derivedFrom":[subQ2,subQ0]});Q33=makeQuery(id+"F9.imprint","IMPRINT",FACE,{"disambiguationData":[TD([[makeQuery(id+"F9.imprint","IMPRINT",EDGE,{"disambiguationData":[TD([[subQ3,-1.0]])],"derivedFrom":subQ0}),1.0]])]});}
            var Q34;
            {var subQ0=sQuery(id+"F9.wireOp",EDGE,"E10.4.5.0");var subQ1=sQuery(id+"F0.wireOp",EDGE,"E0.right");var subQ2=makeQuery(id+"F8.opFillet","BLEND_EDGE",EDGE,{"blendedFrom":[makeQuery(id+"F1.opExtrude","CAP_EDGE",EDGE,{"disambiguationData":[OSD([subQ1])],"isStart":false}),makeQuery(id+"F1.opExtrude","CAP_FACE",FACE,{"disambiguationData":[OSD([sQuery(id+"F0.wireOp",EDGE,"E0.bottom"),sQuery(id+"F0.wireOp",EDGE,"E0.top"),sQuery(id+"F0.wireOp",EDGE,"E0.left"),subQ1,sQuery(id+"F0.wireOp",EDGE,"E5.bottom"),sQuery(id+"F0.wireOp",EDGE,"E5.top"),sQuery(id+"F0.wireOp",EDGE,"E5.left"),sQuery(id+"F0.wireOp",EDGE,"E5.right"),sQuery(id+"F0.wireOp",EDGE,"E6"),sQuery(id+"F0.wireOp",EDGE,"E7.MirrorC")])],"isStart":false})],"blendedInto":[makeQuery(id+"F1.opExtrude","CAP_FACE",FACE,{"disambiguationData":[OSD([sQuery(id+"F0.wireOp",EDGE,"E0.bottom"),sQuery(id+"F0.wireOp",EDGE,"E0.top"),sQuery(id+"F0.wireOp",EDGE,"E0.left"),subQ1,sQuery(id+"F0.wireOp",EDGE,"E5.bottom"),sQuery(id+"F0.wireOp",EDGE,"E5.top"),sQuery(id+"F0.wireOp",EDGE,"E5.left"),sQuery(id+"F0.wireOp",EDGE,"E5.right"),sQuery(id+"F0.wireOp",EDGE,"E6"),sQuery(id+"F0.wireOp",EDGE,"E7.MirrorC")])],"isStart":false})]});var subQ3=makeQuery(id+"F9.imprint","INTERSECT",VERTEX,{"disambiguationData":[OD(0.0)],"derivedFrom":[subQ2,subQ0]});Q34=makeQuery(id+"F9.imprint","IMPRINT",FACE,{"disambiguationData":[TD([[makeQuery(id+"F9.imprint","IMPRINT",EDGE,{"disambiguationData":[TD([[subQ3,-1.0]])],"derivedFrom":subQ0}),1.0]])]});}
            var Q35;
            {var subQ0=sQuery(id+"F9.wireOp",EDGE,"E10.4.6.0");var subQ1=sQuery(id+"F0.wireOp",EDGE,"E0.right");var subQ2=makeQuery(id+"F8.opFillet","BLEND_EDGE",EDGE,{"blendedFrom":[makeQuery(id+"F1.opExtrude","CAP_EDGE",EDGE,{"disambiguationData":[OSD([subQ1])],"isStart":false}),makeQuery(id+"F1.opExtrude","CAP_FACE",FACE,{"disambiguationData":[OSD([sQuery(id+"F0.wireOp",EDGE,"E0.bottom"),sQuery(id+"F0.wireOp",EDGE,"E0.top"),sQuery(id+"F0.wireOp",EDGE,"E0.left"),subQ1,sQuery(id+"F0.wireOp",EDGE,"E5.bottom"),sQuery(id+"F0.wireOp",EDGE,"E5.top"),sQuery(id+"F0.wireOp",EDGE,"E5.left"),sQuery(id+"F0.wireOp",EDGE,"E5.right"),sQuery(id+"F0.wireOp",EDGE,"E6"),sQuery(id+"F0.wireOp",EDGE,"E7.MirrorC")])],"isStart":false})],"blendedInto":[makeQuery(id+"F1.opExtrude","CAP_FACE",FACE,{"disambiguationData":[OSD([sQuery(id+"F0.wireOp",EDGE,"E0.bottom"),sQuery(id+"F0.wireOp",EDGE,"E0.top"),sQuery(id+"F0.wireOp",EDGE,"E0.left"),subQ1,sQuery(id+"F0.wireOp",EDGE,"E5.bottom"),sQuery(id+"F0.wireOp",EDGE,"E5.top"),sQuery(id+"F0.wireOp",EDGE,"E5.left"),sQuery(id+"F0.wireOp",EDGE,"E5.right"),sQuery(id+"F0.wireOp",EDGE,"E6"),sQuery(id+"F0.wireOp",EDGE,"E7.MirrorC")])],"isStart":false})]});var subQ3=makeQuery(id+"F9.imprint","INTERSECT",VERTEX,{"disambiguationData":[OD(0.0)],"derivedFrom":[subQ2,subQ0]});Q35=makeQuery(id+"F9.imprint","IMPRINT",FACE,{"disambiguationData":[TD([[makeQuery(id+"F9.imprint","IMPRINT",EDGE,{"disambiguationData":[TD([[subQ3,-1.0]])],"derivedFrom":subQ0}),1.0]])]});}
            var Q36;
            Q36=makeQuery(id+"F9.imprint","IMPRINT",FACE,{"disambiguationData":[TD([[makeQuery(id+"F9.imprint","IMPRINT",EDGE,{"derivedFrom":sQuery(id+"F9.wireOp",EDGE,"E10.3.7.0")}),1.0]])]});
            var Q37;
            Q37=makeQuery(id+"F9.imprint","IMPRINT",FACE,{"disambiguationData":[TD([[makeQuery(id+"F9.imprint","IMPRINT",EDGE,{"derivedFrom":sQuery(id+"F9.wireOp",EDGE,"E10.2.7.0")}),1.0]])]});
            var Q38;
            Q38=makeQuery(id+"F9.imprint","IMPRINT",FACE,{"disambiguationData":[TD([[makeQuery(id+"F9.imprint","IMPRINT",EDGE,{"derivedFrom":sQuery(id+"F9.wireOp",EDGE,"E10.1.7.0")}),1.0]])]});
            var Q39;
            Q39=makeQuery(id+"F9.imprint","IMPRINT",FACE,{"disambiguationData":[TD([[makeQuery(id+"F9.imprint","IMPRINT",EDGE,{"derivedFrom":sQuery(id+"F9.wireOp",EDGE,"E10.0.7.0")}),1.0]])]});
            var Q40;
            Q40=makeQuery(id+"F9.imprint","IMPRINT",FACE,{"disambiguationData":[TD([[makeQuery(id+"F9.imprint","IMPRINT",EDGE,{"derivedFrom":sQuery(id+"F9.wireOp",EDGE,"E12.1.7.0")}),1.0]])]});
            var Q41;
            Q41=makeQuery(id+"F9.imprint","IMPRINT",FACE,{"disambiguationData":[TD([[makeQuery(id+"F9.imprint","IMPRINT",EDGE,{"derivedFrom":sQuery(id+"F9.wireOp",EDGE,"E12.2.7.0")}),1.0]])]});
            var Q42;
            Q42=makeQuery(id+"F9.imprint","IMPRINT",FACE,{"disambiguationData":[TD([[makeQuery(id+"F9.imprint","IMPRINT",EDGE,{"derivedFrom":sQuery(id+"F9.wireOp",EDGE,"E12.3.7.0")}),1.0]])]});
            var Q43;
            Q43=makeQuery(id+"F9.imprint","IMPRINT",FACE,{"disambiguationData":[TD([[makeQuery(id+"F9.imprint","IMPRINT",EDGE,{"derivedFrom":sQuery(id+"F9.wireOp",EDGE,"E12.3.6.0")}),1.0]])]});
            var Q44;
            Q44=makeQuery(id+"F9.imprint","IMPRINT",FACE,{"disambiguationData":[TD([[makeQuery(id+"F9.imprint","IMPRINT",EDGE,{"derivedFrom":sQuery(id+"F9.wireOp",EDGE,"E12.2.6.0")}),1.0]])]});
            var Q45;
            Q45=makeQuery(id+"F9.imprint","IMPRINT",FACE,{"disambiguationData":[TD([[makeQuery(id+"F9.imprint","IMPRINT",EDGE,{"derivedFrom":sQuery(id+"F9.wireOp",EDGE,"E12.1.6.0")}),1.0]])]});
            var Q46;
            Q46=makeQuery(id+"F9.imprint","IMPRINT",FACE,{"disambiguationData":[TD([[makeQuery(id+"F9.imprint","IMPRINT",EDGE,{"derivedFrom":sQuery(id+"F9.wireOp",EDGE,"E10.0.6.0")}),1.0]])]});
            var Q47;
            Q47=makeQuery(id+"F9.imprint","IMPRINT",FACE,{"disambiguationData":[TD([[makeQuery(id+"F9.imprint","IMPRINT",EDGE,{"derivedFrom":sQuery(id+"F9.wireOp",EDGE,"E10.1.6.0")}),1.0]])]});
            var Q48;
            Q48=makeQuery(id+"F9.imprint","IMPRINT",FACE,{"disambiguationData":[TD([[makeQuery(id+"F9.imprint","IMPRINT",EDGE,{"derivedFrom":sQuery(id+"F9.wireOp",EDGE,"E10.2.6.0")}),1.0]])]});
            var Q49;
            Q49=makeQuery(id+"F9.imprint","IMPRINT",FACE,{"disambiguationData":[TD([[makeQuery(id+"F9.imprint","IMPRINT",EDGE,{"derivedFrom":sQuery(id+"F9.wireOp",EDGE,"E10.3.6.0")}),1.0]])]});
            var Q50;
            Q50=makeQuery(id+"F9.imprint","IMPRINT",FACE,{"disambiguationData":[TD([[makeQuery(id+"F9.imprint","IMPRINT",EDGE,{"derivedFrom":sQuery(id+"F9.wireOp",EDGE,"E10.3.5.0")}),1.0]])]});
            var Q51;
            Q51=makeQuery(id+"F9.imprint","IMPRINT",FACE,{"disambiguationData":[TD([[makeQuery(id+"F9.imprint","IMPRINT",EDGE,{"derivedFrom":sQuery(id+"F9.wireOp",EDGE,"E10.2.5.0")}),1.0]])]});
            var Q52;
            Q52=makeQuery(id+"F9.imprint","IMPRINT",FACE,{"disambiguationData":[TD([[makeQuery(id+"F9.imprint","IMPRINT",EDGE,{"derivedFrom":sQuery(id+"F9.wireOp",EDGE,"E10.1.5.0")}),1.0]])]});
            var Q53;
            Q53=makeQuery(id+"F9.imprint","IMPRINT",FACE,{"disambiguationData":[TD([[makeQuery(id+"F9.imprint","IMPRINT",EDGE,{"derivedFrom":sQuery(id+"F9.wireOp",EDGE,"E10.0.5.0")}),1.0]])]});
            var Q54;
            Q54=makeQuery(id+"F9.imprint","IMPRINT",FACE,{"disambiguationData":[TD([[makeQuery(id+"F9.imprint","IMPRINT",EDGE,{"derivedFrom":sQuery(id+"F9.wireOp",EDGE,"E12.1.5.0")}),1.0]])]});
            var Q55;
            Q55=makeQuery(id+"F9.imprint","IMPRINT",FACE,{"disambiguationData":[TD([[makeQuery(id+"F9.imprint","IMPRINT",EDGE,{"derivedFrom":sQuery(id+"F9.wireOp",EDGE,"E12.2.5.0")}),1.0]])]});
            var Q56;
            Q56=makeQuery(id+"F9.imprint","IMPRINT",FACE,{"disambiguationData":[TD([[makeQuery(id+"F9.imprint","IMPRINT",EDGE,{"derivedFrom":sQuery(id+"F9.wireOp",EDGE,"E12.3.5.0")}),1.0]])]});
            var Q57;
            Q57=makeQuery(id+"F9.imprint","IMPRINT",FACE,{"disambiguationData":[TD([[makeQuery(id+"F9.imprint","IMPRINT",EDGE,{"derivedFrom":sQuery(id+"F9.wireOp",EDGE,"E12.3.4.0")}),1.0]])]});
            var Q58;
            Q58=makeQuery(id+"F9.imprint","IMPRINT",FACE,{"disambiguationData":[TD([[makeQuery(id+"F9.imprint","IMPRINT",EDGE,{"derivedFrom":sQuery(id+"F9.wireOp",EDGE,"E12.2.4.0")}),1.0]])]});
            var Q59;
            Q59=makeQuery(id+"F9.imprint","IMPRINT",FACE,{"disambiguationData":[TD([[makeQuery(id+"F9.imprint","IMPRINT",EDGE,{"derivedFrom":sQuery(id+"F9.wireOp",EDGE,"E12.1.4.0")}),1.0]])]});
            var Q60;
            Q60=makeQuery(id+"F9.imprint","IMPRINT",FACE,{"disambiguationData":[TD([[makeQuery(id+"F9.imprint","IMPRINT",EDGE,{"derivedFrom":sQuery(id+"F9.wireOp",EDGE,"E10.1.4.0")}),1.0]])]});
            var Q61;
            Q61=makeQuery(id+"F9.imprint","IMPRINT",FACE,{"disambiguationData":[TD([[makeQuery(id+"F9.imprint","IMPRINT",EDGE,{"derivedFrom":sQuery(id+"F9.wireOp",EDGE,"E10.2.4.0")}),1.0]])]});
            var Q62;
            Q62=makeQuery(id+"F9.imprint","IMPRINT",FACE,{"disambiguationData":[TD([[makeQuery(id+"F9.imprint","IMPRINT",EDGE,{"derivedFrom":sQuery(id+"F9.wireOp",EDGE,"E10.3.4.0")}),1.0]])]});
            var Q63;
            Q63=makeQuery(id+"F9.imprint","IMPRINT",FACE,{"disambiguationData":[TD([[makeQuery(id+"F9.imprint","IMPRINT",EDGE,{"derivedFrom":sQuery(id+"F9.wireOp",EDGE,"E10.3.3.0")}),1.0]])]});
            var Q64;
            Q64=makeQuery(id+"F9.imprint","IMPRINT",FACE,{"disambiguationData":[TD([[makeQuery(id+"F9.imprint","IMPRINT",EDGE,{"derivedFrom":sQuery(id+"F9.wireOp",EDGE,"E10.2.3.0")}),1.0]])]});
            var Q65;
            Q65=makeQuery(id+"F9.imprint","IMPRINT",FACE,{"disambiguationData":[TD([[makeQuery(id+"F9.imprint","IMPRINT",EDGE,{"derivedFrom":sQuery(id+"F9.wireOp",EDGE,"E10.1.3.0")}),1.0]])]});
            var Q66;
            {var subQ0=sQuery(id+"F9.wireOp",EDGE,"E10.0.3.0");var subQ1=sQuery(id+"F0.wireOp",EDGE,"E7.MirrorC");var subQ2=makeQuery(id+"F2.opChamfer","BLEND_EDGE",EDGE,{"blendedFrom":[makeQuery(id+"F1.opExtrude","CAP_EDGE",EDGE,{"disambiguationData":[OSD([subQ1])],"isStart":false}),makeQuery(id+"F1.opExtrude","CAP_FACE",FACE,{"disambiguationData":[OSD([sQuery(id+"F0.wireOp",EDGE,"E0.bottom"),sQuery(id+"F0.wireOp",EDGE,"E0.top"),sQuery(id+"F0.wireOp",EDGE,"E0.left"),sQuery(id+"F0.wireOp",EDGE,"E0.right"),sQuery(id+"F0.wireOp",EDGE,"E5.bottom"),sQuery(id+"F0.wireOp",EDGE,"E5.top"),sQuery(id+"F0.wireOp",EDGE,"E5.left"),sQuery(id+"F0.wireOp",EDGE,"E5.right"),sQuery(id+"F0.wireOp",EDGE,"E6"),subQ1])],"isStart":false})],"blendedInto":[makeQuery(id+"F1.opExtrude","CAP_FACE",FACE,{"disambiguationData":[OSD([sQuery(id+"F0.wireOp",EDGE,"E0.bottom"),sQuery(id+"F0.wireOp",EDGE,"E0.top"),sQuery(id+"F0.wireOp",EDGE,"E0.left"),sQuery(id+"F0.wireOp",EDGE,"E0.right"),sQuery(id+"F0.wireOp",EDGE,"E5.bottom"),sQuery(id+"F0.wireOp",EDGE,"E5.top"),sQuery(id+"F0.wireOp",EDGE,"E5.left"),sQuery(id+"F0.wireOp",EDGE,"E5.right"),sQuery(id+"F0.wireOp",EDGE,"E6"),subQ1])],"isStart":false})]});var subQ3=makeQuery(id+"F9.imprint","INTERSECT",VERTEX,{"disambiguationData":[OD(0.0)],"derivedFrom":[subQ2,subQ0]});Q66=makeQuery(id+"F9.imprint","IMPRINT",FACE,{"disambiguationData":[TD([[makeQuery(id+"F9.imprint","IMPRINT",EDGE,{"disambiguationData":[TD([[subQ3,-1.0]])],"derivedFrom":subQ0}),1.0]])]});}
            var Q67;
            Q67=makeQuery(id+"F9.imprint","IMPRINT",FACE,{"disambiguationData":[TD([[makeQuery(id+"F9.imprint","IMPRINT",EDGE,{"derivedFrom":sQuery(id+"F9.wireOp",EDGE,"E12.1.3.0")}),1.0]])]});
            var Q68;
            Q68=makeQuery(id+"F9.imprint","IMPRINT",FACE,{"disambiguationData":[TD([[makeQuery(id+"F9.imprint","IMPRINT",EDGE,{"derivedFrom":sQuery(id+"F9.wireOp",EDGE,"E12.2.3.0")}),1.0]])]});
            var Q69;
            Q69=makeQuery(id+"F9.imprint","IMPRINT",FACE,{"disambiguationData":[TD([[makeQuery(id+"F9.imprint","IMPRINT",EDGE,{"derivedFrom":sQuery(id+"F9.wireOp",EDGE,"E12.3.3.0")}),1.0]])]});
            var Q70;
            Q70=makeQuery(id+"F9.imprint","IMPRINT",FACE,{"disambiguationData":[TD([[makeQuery(id+"F9.imprint","IMPRINT",EDGE,{"derivedFrom":sQuery(id+"F9.wireOp",EDGE,"E12.3.2.0")}),1.0]])]});
            var Q71;
            Q71=makeQuery(id+"F9.imprint","IMPRINT",FACE,{"disambiguationData":[TD([[makeQuery(id+"F9.imprint","IMPRINT",EDGE,{"derivedFrom":sQuery(id+"F9.wireOp",EDGE,"E12.2.2.0")}),1.0]])]});
            var Q72;
            Q72=makeQuery(id+"F9.imprint","IMPRINT",FACE,{"disambiguationData":[TD([[makeQuery(id+"F9.imprint","IMPRINT",EDGE,{"derivedFrom":sQuery(id+"F9.wireOp",EDGE,"E12.1.2.0")}),1.0]])]});
            var Q73;
            Q73=makeQuery(id+"F9.imprint","IMPRINT",FACE,{"disambiguationData":[TD([[makeQuery(id+"F9.imprint","IMPRINT",EDGE,{"derivedFrom":sQuery(id+"F9.wireOp",EDGE,"E10.0.2.0")}),1.0]])]});
            var Q74;
            Q74=makeQuery(id+"F9.imprint","IMPRINT",FACE,{"disambiguationData":[TD([[makeQuery(id+"F9.imprint","IMPRINT",EDGE,{"derivedFrom":sQuery(id+"F9.wireOp",EDGE,"E10.1.2.0")}),1.0]])]});
            var Q75;
            Q75=makeQuery(id+"F9.imprint","IMPRINT",FACE,{"disambiguationData":[TD([[makeQuery(id+"F9.imprint","IMPRINT",EDGE,{"derivedFrom":sQuery(id+"F9.wireOp",EDGE,"E10.2.2.0")}),1.0]])]});
            var Q76;
            Q76=makeQuery(id+"F9.imprint","IMPRINT",FACE,{"disambiguationData":[TD([[makeQuery(id+"F9.imprint","IMPRINT",EDGE,{"derivedFrom":sQuery(id+"F9.wireOp",EDGE,"E10.3.2.0")}),1.0]])]});
            var Q77;
            Q77=makeQuery(id+"F9.imprint","IMPRINT",FACE,{"disambiguationData":[TD([[makeQuery(id+"F9.imprint","IMPRINT",EDGE,{"derivedFrom":sQuery(id+"F9.wireOp",EDGE,"E10.3.1.0")}),1.0]])]});
            var Q78;
            Q78=makeQuery(id+"F9.imprint","IMPRINT",FACE,{"disambiguationData":[TD([[makeQuery(id+"F9.imprint","IMPRINT",EDGE,{"derivedFrom":sQuery(id+"F9.wireOp",EDGE,"E10.2.1.0")}),1.0]])]});
            var Q79;
            {var subQ0=sQuery(id+"F9.wireOp",EDGE,"E10.1.1.0");var subQ1=sQuery(id+"F0.wireOp",EDGE,"E5.right");var subQ2=makeQuery(id+"F3.opChamfer","BLEND_EDGE",EDGE,{"blendedFrom":[makeQuery(id+"F1.opExtrude","CAP_EDGE",EDGE,{"disambiguationData":[OSD([subQ1])],"isStart":false}),makeQuery(id+"F1.opExtrude","CAP_FACE",FACE,{"disambiguationData":[OSD([sQuery(id+"F0.wireOp",EDGE,"E0.bottom"),sQuery(id+"F0.wireOp",EDGE,"E0.top"),sQuery(id+"F0.wireOp",EDGE,"E0.left"),sQuery(id+"F0.wireOp",EDGE,"E0.right"),sQuery(id+"F0.wireOp",EDGE,"E5.bottom"),sQuery(id+"F0.wireOp",EDGE,"E5.top"),sQuery(id+"F0.wireOp",EDGE,"E5.left"),subQ1,sQuery(id+"F0.wireOp",EDGE,"E6"),sQuery(id+"F0.wireOp",EDGE,"E7.MirrorC")])],"isStart":false})],"blendedInto":[makeQuery(id+"F1.opExtrude","CAP_FACE",FACE,{"disambiguationData":[OSD([sQuery(id+"F0.wireOp",EDGE,"E0.bottom"),sQuery(id+"F0.wireOp",EDGE,"E0.top"),sQuery(id+"F0.wireOp",EDGE,"E0.left"),sQuery(id+"F0.wireOp",EDGE,"E0.right"),sQuery(id+"F0.wireOp",EDGE,"E5.bottom"),sQuery(id+"F0.wireOp",EDGE,"E5.top"),sQuery(id+"F0.wireOp",EDGE,"E5.left"),subQ1,sQuery(id+"F0.wireOp",EDGE,"E6"),sQuery(id+"F0.wireOp",EDGE,"E7.MirrorC")])],"isStart":false})]});var subQ3=makeQuery(id+"F9.imprint","INTERSECT",VERTEX,{"disambiguationData":[OD(0.0)],"derivedFrom":[subQ2,subQ0]});Q79=makeQuery(id+"F9.imprint","IMPRINT",FACE,{"disambiguationData":[TD([[makeQuery(id+"F9.imprint","IMPRINT",EDGE,{"disambiguationData":[TD([[subQ3,1.0]])],"derivedFrom":subQ0}),1.0]])]});}
            var Q80;
            {var subQ0=sQuery(id+"F9.wireOp",EDGE,"E12.1.1.0");var subQ1=sQuery(id+"F0.wireOp",EDGE,"E5.left");var subQ2=makeQuery(id+"F3.opChamfer","BLEND_EDGE",EDGE,{"blendedFrom":[makeQuery(id+"F1.opExtrude","CAP_EDGE",EDGE,{"disambiguationData":[OSD([subQ1])],"isStart":false}),makeQuery(id+"F1.opExtrude","CAP_FACE",FACE,{"disambiguationData":[OSD([sQuery(id+"F0.wireOp",EDGE,"E0.bottom"),sQuery(id+"F0.wireOp",EDGE,"E0.top"),sQuery(id+"F0.wireOp",EDGE,"E0.left"),sQuery(id+"F0.wireOp",EDGE,"E0.right"),sQuery(id+"F0.wireOp",EDGE,"E5.bottom"),sQuery(id+"F0.wireOp",EDGE,"E5.top"),subQ1,sQuery(id+"F0.wireOp",EDGE,"E5.right"),sQuery(id+"F0.wireOp",EDGE,"E6"),sQuery(id+"F0.wireOp",EDGE,"E7.MirrorC")])],"isStart":false})],"blendedInto":[makeQuery(id+"F1.opExtrude","CAP_FACE",FACE,{"disambiguationData":[OSD([sQuery(id+"F0.wireOp",EDGE,"E0.bottom"),sQuery(id+"F0.wireOp",EDGE,"E0.top"),sQuery(id+"F0.wireOp",EDGE,"E0.left"),sQuery(id+"F0.wireOp",EDGE,"E0.right"),sQuery(id+"F0.wireOp",EDGE,"E5.bottom"),sQuery(id+"F0.wireOp",EDGE,"E5.top"),subQ1,sQuery(id+"F0.wireOp",EDGE,"E5.right"),sQuery(id+"F0.wireOp",EDGE,"E6"),sQuery(id+"F0.wireOp",EDGE,"E7.MirrorC")])],"isStart":false})]});var subQ3=makeQuery(id+"F9.imprint","INTERSECT",VERTEX,{"disambiguationData":[OD(0.0)],"derivedFrom":[subQ2,subQ0]});Q80=makeQuery(id+"F9.imprint","IMPRINT",FACE,{"disambiguationData":[TD([[makeQuery(id+"F9.imprint","IMPRINT",EDGE,{"disambiguationData":[TD([[subQ3,-1.0]])],"derivedFrom":subQ0}),1.0]])]});}
            var Q81;
            Q81=makeQuery(id+"F9.imprint","IMPRINT",FACE,{"disambiguationData":[TD([[makeQuery(id+"F9.imprint","IMPRINT",EDGE,{"derivedFrom":sQuery(id+"F9.wireOp",EDGE,"E12.2.1.0")}),1.0]])]});
            var Q82;
            Q82=makeQuery(id+"F9.imprint","IMPRINT",FACE,{"disambiguationData":[TD([[makeQuery(id+"F9.imprint","IMPRINT",EDGE,{"derivedFrom":sQuery(id+"F9.wireOp",EDGE,"E12.3.1.0")}),1.0]])]});
            var Q83;
            Q83=makeQuery(id+"F9.imprint","IMPRINT",FACE,{"disambiguationData":[TD([[makeQuery(id+"F9.imprint","IMPRINT",EDGE,{"derivedFrom":sQuery(id+"F9.wireOp",EDGE,"E11.0.3.0")}),1.0]])]});
            var Q84;
            Q84=makeQuery(id+"F9.imprint","IMPRINT",FACE,{"disambiguationData":[TD([[makeQuery(id+"F9.imprint","IMPRINT",EDGE,{"derivedFrom":sQuery(id+"F9.wireOp",EDGE,"E11.0.2.0")}),1.0]])]});
            var Q85;
            {var subQ0=sQuery(id+"F9.wireOp",EDGE,"E11.0.1.0");var subQ1=sQuery(id+"F0.wireOp",EDGE,"E5.left");var subQ2=makeQuery(id+"F3.opChamfer","BLEND_EDGE",EDGE,{"blendedFrom":[makeQuery(id+"F1.opExtrude","CAP_EDGE",EDGE,{"disambiguationData":[OSD([subQ1])],"isStart":false}),makeQuery(id+"F1.opExtrude","CAP_FACE",FACE,{"disambiguationData":[OSD([sQuery(id+"F0.wireOp",EDGE,"E0.bottom"),sQuery(id+"F0.wireOp",EDGE,"E0.top"),sQuery(id+"F0.wireOp",EDGE,"E0.left"),sQuery(id+"F0.wireOp",EDGE,"E0.right"),sQuery(id+"F0.wireOp",EDGE,"E5.bottom"),sQuery(id+"F0.wireOp",EDGE,"E5.top"),subQ1,sQuery(id+"F0.wireOp",EDGE,"E5.right"),sQuery(id+"F0.wireOp",EDGE,"E6"),sQuery(id+"F0.wireOp",EDGE,"E7.MirrorC")])],"isStart":false})],"blendedInto":[makeQuery(id+"F1.opExtrude","CAP_FACE",FACE,{"disambiguationData":[OSD([sQuery(id+"F0.wireOp",EDGE,"E0.bottom"),sQuery(id+"F0.wireOp",EDGE,"E0.top"),sQuery(id+"F0.wireOp",EDGE,"E0.left"),sQuery(id+"F0.wireOp",EDGE,"E0.right"),sQuery(id+"F0.wireOp",EDGE,"E5.bottom"),sQuery(id+"F0.wireOp",EDGE,"E5.top"),subQ1,sQuery(id+"F0.wireOp",EDGE,"E5.right"),sQuery(id+"F0.wireOp",EDGE,"E6"),sQuery(id+"F0.wireOp",EDGE,"E7.MirrorC")])],"isStart":false})]});var subQ3=makeQuery(id+"F9.imprint","INTERSECT",VERTEX,{"disambiguationData":[OD(0.0)],"derivedFrom":[subQ2,subQ0]});Q85=makeQuery(id+"F9.imprint","IMPRINT",FACE,{"disambiguationData":[TD([[makeQuery(id+"F9.imprint","IMPRINT",EDGE,{"disambiguationData":[TD([[subQ3,1.0]])],"derivedFrom":subQ0}),1.0]])]});}
            var Q86;
            {var subQ0=sQuery(id+"F9.wireOp",EDGE,"E10.1.0.0");var subQ1=sQuery(id+"F0.wireOp",EDGE,"E5.right");var subQ2=makeQuery(id+"F3.opChamfer","BLEND_EDGE",EDGE,{"blendedFrom":[makeQuery(id+"F1.opExtrude","CAP_EDGE",EDGE,{"disambiguationData":[OSD([subQ1])],"isStart":false}),makeQuery(id+"F1.opExtrude","CAP_FACE",FACE,{"disambiguationData":[OSD([sQuery(id+"F0.wireOp",EDGE,"E0.bottom"),sQuery(id+"F0.wireOp",EDGE,"E0.top"),sQuery(id+"F0.wireOp",EDGE,"E0.left"),sQuery(id+"F0.wireOp",EDGE,"E0.right"),sQuery(id+"F0.wireOp",EDGE,"E5.bottom"),sQuery(id+"F0.wireOp",EDGE,"E5.top"),sQuery(id+"F0.wireOp",EDGE,"E5.left"),subQ1,sQuery(id+"F0.wireOp",EDGE,"E6"),sQuery(id+"F0.wireOp",EDGE,"E7.MirrorC")])],"isStart":false})],"blendedInto":[makeQuery(id+"F1.opExtrude","CAP_FACE",FACE,{"disambiguationData":[OSD([sQuery(id+"F0.wireOp",EDGE,"E0.bottom"),sQuery(id+"F0.wireOp",EDGE,"E0.top"),sQuery(id+"F0.wireOp",EDGE,"E0.left"),sQuery(id+"F0.wireOp",EDGE,"E0.right"),sQuery(id+"F0.wireOp",EDGE,"E5.bottom"),sQuery(id+"F0.wireOp",EDGE,"E5.top"),sQuery(id+"F0.wireOp",EDGE,"E5.left"),subQ1,sQuery(id+"F0.wireOp",EDGE,"E6"),sQuery(id+"F0.wireOp",EDGE,"E7.MirrorC")])],"isStart":false})]});var subQ3=makeQuery(id+"F9.imprint","INTERSECT",VERTEX,{"disambiguationData":[OD(0.0)],"derivedFrom":[subQ2,subQ0]});Q86=makeQuery(id+"F9.imprint","IMPRINT",FACE,{"disambiguationData":[TD([[makeQuery(id+"F9.imprint","IMPRINT",EDGE,{"disambiguationData":[TD([[subQ3,1.0]])],"derivedFrom":subQ0}),1.0]])]});}
            var Q87;
            Q87=makeQuery(id+"F9.imprint","IMPRINT",FACE,{"disambiguationData":[TD([[makeQuery(id+"F9.imprint","IMPRINT",EDGE,{"derivedFrom":sQuery(id+"F9.wireOp",EDGE,"E10.2.0.0")}),1.0]])]});
            var Q88;
            Q88=makeQuery(id+"F9.imprint","IMPRINT",FACE,{"disambiguationData":[TD([[makeQuery(id+"F9.imprint","IMPRINT",EDGE,{"derivedFrom":sQuery(id+"F9.wireOp",EDGE,"E10.3.0.0")}),1.0]])]});
            var Q89;
            Q89=makeQuery(id+"F9.imprint","IMPRINT",FACE,{"disambiguationData":[TD([[makeQuery(id+"F9.imprint","IMPRINT",EDGE,{"derivedFrom":sQuery(id+"F9.wireOp",EDGE,"E13.3.1.0")}),1.0]])]});
            var Q90;
            Q90=makeQuery(id+"F9.imprint","IMPRINT",FACE,{"disambiguationData":[TD([[makeQuery(id+"F9.imprint","IMPRINT",EDGE,{"derivedFrom":sQuery(id+"F9.wireOp",EDGE,"E13.2.1.0")}),1.0]])]});
            var Q91;
            {var subQ0=sQuery(id+"F9.wireOp",EDGE,"E13.1.1.0");var subQ1=sQuery(id+"F0.wireOp",EDGE,"E5.right");var subQ2=makeQuery(id+"F3.opChamfer","BLEND_EDGE",EDGE,{"blendedFrom":[makeQuery(id+"F1.opExtrude","CAP_EDGE",EDGE,{"disambiguationData":[OSD([subQ1])],"isStart":false}),makeQuery(id+"F1.opExtrude","CAP_FACE",FACE,{"disambiguationData":[OSD([sQuery(id+"F0.wireOp",EDGE,"E0.bottom"),sQuery(id+"F0.wireOp",EDGE,"E0.top"),sQuery(id+"F0.wireOp",EDGE,"E0.left"),sQuery(id+"F0.wireOp",EDGE,"E0.right"),sQuery(id+"F0.wireOp",EDGE,"E5.bottom"),sQuery(id+"F0.wireOp",EDGE,"E5.top"),sQuery(id+"F0.wireOp",EDGE,"E5.left"),subQ1,sQuery(id+"F0.wireOp",EDGE,"E6"),sQuery(id+"F0.wireOp",EDGE,"E7.MirrorC")])],"isStart":false})],"blendedInto":[makeQuery(id+"F1.opExtrude","CAP_FACE",FACE,{"disambiguationData":[OSD([sQuery(id+"F0.wireOp",EDGE,"E0.bottom"),sQuery(id+"F0.wireOp",EDGE,"E0.top"),sQuery(id+"F0.wireOp",EDGE,"E0.left"),sQuery(id+"F0.wireOp",EDGE,"E0.right"),sQuery(id+"F0.wireOp",EDGE,"E5.bottom"),sQuery(id+"F0.wireOp",EDGE,"E5.top"),sQuery(id+"F0.wireOp",EDGE,"E5.left"),subQ1,sQuery(id+"F0.wireOp",EDGE,"E6"),sQuery(id+"F0.wireOp",EDGE,"E7.MirrorC")])],"isStart":false})]});var subQ3=makeQuery(id+"F9.imprint","INTERSECT",VERTEX,{"disambiguationData":[OD(0.0)],"derivedFrom":[subQ2,subQ0]});Q91=makeQuery(id+"F9.imprint","IMPRINT",FACE,{"disambiguationData":[TD([[makeQuery(id+"F9.imprint","IMPRINT",EDGE,{"disambiguationData":[TD([[subQ3,-1.0]])],"derivedFrom":subQ0}),1.0]])]});}
            var Q92;
            {var subQ0=sQuery(id+"F9.wireOp",EDGE,"E11.1.1.0");var subQ1=sQuery(id+"F0.wireOp",EDGE,"E5.left");var subQ2=makeQuery(id+"F3.opChamfer","BLEND_EDGE",EDGE,{"blendedFrom":[makeQuery(id+"F1.opExtrude","CAP_EDGE",EDGE,{"disambiguationData":[OSD([subQ1])],"isStart":false}),makeQuery(id+"F1.opExtrude","CAP_FACE",FACE,{"disambiguationData":[OSD([sQuery(id+"F0.wireOp",EDGE,"E0.bottom"),sQuery(id+"F0.wireOp",EDGE,"E0.top"),sQuery(id+"F0.wireOp",EDGE,"E0.left"),sQuery(id+"F0.wireOp",EDGE,"E0.right"),sQuery(id+"F0.wireOp",EDGE,"E5.bottom"),sQuery(id+"F0.wireOp",EDGE,"E5.top"),subQ1,sQuery(id+"F0.wireOp",EDGE,"E5.right"),sQuery(id+"F0.wireOp",EDGE,"E6"),sQuery(id+"F0.wireOp",EDGE,"E7.MirrorC")])],"isStart":false})],"blendedInto":[makeQuery(id+"F1.opExtrude","CAP_FACE",FACE,{"disambiguationData":[OSD([sQuery(id+"F0.wireOp",EDGE,"E0.bottom"),sQuery(id+"F0.wireOp",EDGE,"E0.top"),sQuery(id+"F0.wireOp",EDGE,"E0.left"),sQuery(id+"F0.wireOp",EDGE,"E0.right"),sQuery(id+"F0.wireOp",EDGE,"E5.bottom"),sQuery(id+"F0.wireOp",EDGE,"E5.top"),subQ1,sQuery(id+"F0.wireOp",EDGE,"E5.right"),sQuery(id+"F0.wireOp",EDGE,"E6"),sQuery(id+"F0.wireOp",EDGE,"E7.MirrorC")])],"isStart":false})]});var subQ3=makeQuery(id+"F9.imprint","INTERSECT",VERTEX,{"disambiguationData":[OD(0.0)],"derivedFrom":[subQ2,subQ0]});Q92=makeQuery(id+"F9.imprint","IMPRINT",FACE,{"disambiguationData":[TD([[makeQuery(id+"F9.imprint","IMPRINT",EDGE,{"disambiguationData":[TD([[subQ3,1.0]])],"derivedFrom":subQ0}),1.0]])]});}
            var Q93;
            Q93=makeQuery(id+"F9.imprint","IMPRINT",FACE,{"disambiguationData":[TD([[makeQuery(id+"F9.imprint","IMPRINT",EDGE,{"derivedFrom":sQuery(id+"F9.wireOp",EDGE,"E11.1.2.0")}),1.0]])]});
            var Q94;
            Q94=makeQuery(id+"F9.imprint","IMPRINT",FACE,{"disambiguationData":[TD([[makeQuery(id+"F9.imprint","IMPRINT",EDGE,{"derivedFrom":sQuery(id+"F9.wireOp",EDGE,"E11.1.3.0")}),1.0]])]});
            var Q95;
            Q95=makeQuery(id+"F9.imprint","IMPRINT",FACE,{"disambiguationData":[TD([[makeQuery(id+"F9.imprint","IMPRINT",EDGE,{"derivedFrom":sQuery(id+"F9.wireOp",EDGE,"E11.2.3.0")}),1.0]])]});
            var Q96;
            Q96=makeQuery(id+"F9.imprint","IMPRINT",FACE,{"disambiguationData":[TD([[makeQuery(id+"F9.imprint","IMPRINT",EDGE,{"derivedFrom":sQuery(id+"F9.wireOp",EDGE,"E11.2.2.0")}),1.0]])]});
            var Q97;
            Q97=makeQuery(id+"F9.imprint","IMPRINT",FACE,{"disambiguationData":[TD([[makeQuery(id+"F9.imprint","IMPRINT",EDGE,{"derivedFrom":sQuery(id+"F9.wireOp",EDGE,"E11.2.1.0")}),1.0]])]});
            var Q98;
            Q98=makeQuery(id+"F9.imprint","IMPRINT",FACE,{"disambiguationData":[TD([[makeQuery(id+"F9.imprint","IMPRINT",EDGE,{"derivedFrom":sQuery(id+"F9.wireOp",EDGE,"E11.2.0.0")}),1.0]])]});
            var Q99;
            Q99=makeQuery(id+"F9.imprint","IMPRINT",FACE,{"disambiguationData":[TD([[makeQuery(id+"F9.imprint","IMPRINT",EDGE,{"derivedFrom":sQuery(id+"F9.wireOp",EDGE,"E13.1.2.0")}),1.0]])]});
            var Q100;
            Q100=makeQuery(id+"F9.imprint","IMPRINT",FACE,{"disambiguationData":[TD([[makeQuery(id+"F9.imprint","IMPRINT",EDGE,{"derivedFrom":sQuery(id+"F9.wireOp",EDGE,"E13.2.2.0")}),1.0]])]});
            var Q101;
            Q101=makeQuery(id+"F9.imprint","IMPRINT",FACE,{"disambiguationData":[TD([[makeQuery(id+"F9.imprint","IMPRINT",EDGE,{"derivedFrom":sQuery(id+"F9.wireOp",EDGE,"E13.3.2.0")}),1.0]])]});
            var Q102;
            Q102=makeQuery(id+"F9.imprint","IMPRINT",FACE,{"disambiguationData":[TD([[makeQuery(id+"F9.imprint","IMPRINT",EDGE,{"derivedFrom":sQuery(id+"F9.wireOp",EDGE,"E13.3.3.0")}),1.0]])]});
            var Q103;
            Q103=makeQuery(id+"F9.imprint","IMPRINT",FACE,{"disambiguationData":[TD([[makeQuery(id+"F9.imprint","IMPRINT",EDGE,{"derivedFrom":sQuery(id+"F9.wireOp",EDGE,"E13.2.3.0")}),1.0]])]});
            var Q104;
            Q104=makeQuery(id+"F9.imprint","IMPRINT",FACE,{"disambiguationData":[TD([[makeQuery(id+"F9.imprint","IMPRINT",EDGE,{"derivedFrom":sQuery(id+"F9.wireOp",EDGE,"E13.1.3.0")}),1.0]])]});
            var Q105;
            {var subQ0=sQuery(id+"F9.wireOp",EDGE,"E11.3.0.0");var subQ1=sQuery(id+"F0.wireOp",EDGE,"E6");var subQ2=makeQuery(id+"F2.opChamfer","BLEND_EDGE",EDGE,{"blendedFrom":[makeQuery(id+"F1.opExtrude","CAP_EDGE",EDGE,{"disambiguationData":[OSD([subQ1])],"isStart":false}),makeQuery(id+"F1.opExtrude","CAP_FACE",FACE,{"disambiguationData":[OSD([sQuery(id+"F0.wireOp",EDGE,"E0.bottom"),sQuery(id+"F0.wireOp",EDGE,"E0.top"),sQuery(id+"F0.wireOp",EDGE,"E0.left"),sQuery(id+"F0.wireOp",EDGE,"E0.right"),sQuery(id+"F0.wireOp",EDGE,"E5.bottom"),sQuery(id+"F0.wireOp",EDGE,"E5.top"),sQuery(id+"F0.wireOp",EDGE,"E5.left"),sQuery(id+"F0.wireOp",EDGE,"E5.right"),subQ1,sQuery(id+"F0.wireOp",EDGE,"E7.MirrorC")])],"isStart":false})],"blendedInto":[makeQuery(id+"F1.opExtrude","CAP_FACE",FACE,{"disambiguationData":[OSD([sQuery(id+"F0.wireOp",EDGE,"E0.bottom"),sQuery(id+"F0.wireOp",EDGE,"E0.top"),sQuery(id+"F0.wireOp",EDGE,"E0.left"),sQuery(id+"F0.wireOp",EDGE,"E0.right"),sQuery(id+"F0.wireOp",EDGE,"E5.bottom"),sQuery(id+"F0.wireOp",EDGE,"E5.top"),sQuery(id+"F0.wireOp",EDGE,"E5.left"),sQuery(id+"F0.wireOp",EDGE,"E5.right"),subQ1,sQuery(id+"F0.wireOp",EDGE,"E7.MirrorC")])],"isStart":false})]});var subQ3=makeQuery(id+"F9.imprint","INTERSECT",VERTEX,{"disambiguationData":[OD(0.0)],"derivedFrom":[subQ2,subQ0]});Q105=makeQuery(id+"F9.imprint","IMPRINT",FACE,{"disambiguationData":[TD([[makeQuery(id+"F9.imprint","IMPRINT",EDGE,{"disambiguationData":[TD([[subQ3,1.0]])],"derivedFrom":subQ0}),1.0]])]});}
            var Q106;
            Q106=makeQuery(id+"F9.imprint","IMPRINT",FACE,{"disambiguationData":[TD([[makeQuery(id+"F9.imprint","IMPRINT",EDGE,{"derivedFrom":sQuery(id+"F9.wireOp",EDGE,"E11.3.1.0")}),1.0]])]});
            var Q107;
            Q107=makeQuery(id+"F9.imprint","IMPRINT",FACE,{"disambiguationData":[TD([[makeQuery(id+"F9.imprint","IMPRINT",EDGE,{"derivedFrom":sQuery(id+"F9.wireOp",EDGE,"E11.3.2.0")}),1.0]])]});
            var Q108;
            Q108=makeQuery(id+"F9.imprint","IMPRINT",FACE,{"disambiguationData":[TD([[makeQuery(id+"F9.imprint","IMPRINT",EDGE,{"derivedFrom":sQuery(id+"F9.wireOp",EDGE,"E11.3.3.0")}),1.0]])]});
            var Q109;
            Q109=makeQuery(id+"F9.imprint","IMPRINT",FACE,{"disambiguationData":[TD([[makeQuery(id+"F9.imprint","IMPRINT",EDGE,{"derivedFrom":sQuery(id+"F9.wireOp",EDGE,"E11.4.3.0")}),1.0]])]});
            var Q110;
            Q110=makeQuery(id+"F9.imprint","IMPRINT",FACE,{"disambiguationData":[TD([[makeQuery(id+"F9.imprint","IMPRINT",EDGE,{"derivedFrom":sQuery(id+"F9.wireOp",EDGE,"E11.4.2.0")}),1.0]])]});
            var Q111;
            Q111=makeQuery(id+"F9.imprint","IMPRINT",FACE,{"disambiguationData":[TD([[makeQuery(id+"F9.imprint","IMPRINT",EDGE,{"derivedFrom":sQuery(id+"F9.wireOp",EDGE,"E11.4.1.0")}),1.0]])]});
            var Q112;
            Q112=makeQuery(id+"F9.imprint","IMPRINT",FACE,{"disambiguationData":[TD([[makeQuery(id+"F9.imprint","IMPRINT",EDGE,{"derivedFrom":sQuery(id+"F9.wireOp",EDGE,"E13.1.4.0")}),1.0]])]});
            var Q113;
            Q113=makeQuery(id+"F9.imprint","IMPRINT",FACE,{"disambiguationData":[TD([[makeQuery(id+"F9.imprint","IMPRINT",EDGE,{"derivedFrom":sQuery(id+"F9.wireOp",EDGE,"E13.2.4.0")}),1.0]])]});
            var Q114;
            Q114=makeQuery(id+"F9.imprint","IMPRINT",FACE,{"disambiguationData":[TD([[makeQuery(id+"F9.imprint","IMPRINT",EDGE,{"derivedFrom":sQuery(id+"F9.wireOp",EDGE,"E13.3.4.0")}),1.0]])]});
            var Q115;
            Q115=makeQuery(id+"F9.imprint","IMPRINT",FACE,{"disambiguationData":[TD([[makeQuery(id+"F9.imprint","IMPRINT",EDGE,{"derivedFrom":sQuery(id+"F9.wireOp",EDGE,"E13.3.5.0")}),1.0]])]});
            var Q116;
            Q116=makeQuery(id+"F9.imprint","IMPRINT",FACE,{"disambiguationData":[TD([[makeQuery(id+"F9.imprint","IMPRINT",EDGE,{"derivedFrom":sQuery(id+"F9.wireOp",EDGE,"E13.2.5.0")}),1.0]])]});
            var Q117;
            Q117=makeQuery(id+"F9.imprint","IMPRINT",FACE,{"disambiguationData":[TD([[makeQuery(id+"F9.imprint","IMPRINT",EDGE,{"derivedFrom":sQuery(id+"F9.wireOp",EDGE,"E13.1.5.0")}),1.0]])]});
            var Q118;
            Q118=makeQuery(id+"F9.imprint","IMPRINT",FACE,{"disambiguationData":[TD([[makeQuery(id+"F9.imprint","IMPRINT",EDGE,{"derivedFrom":sQuery(id+"F9.wireOp",EDGE,"E11.5.0.0")}),1.0]])]});
            var Q119;
            Q119=makeQuery(id+"F9.imprint","IMPRINT",FACE,{"disambiguationData":[TD([[makeQuery(id+"F9.imprint","IMPRINT",EDGE,{"derivedFrom":sQuery(id+"F9.wireOp",EDGE,"E11.5.1.0")}),1.0]])]});
            var Q120;
            Q120=makeQuery(id+"F9.imprint","IMPRINT",FACE,{"disambiguationData":[TD([[makeQuery(id+"F9.imprint","IMPRINT",EDGE,{"derivedFrom":sQuery(id+"F9.wireOp",EDGE,"E11.5.2.0")}),1.0]])]});
            var Q121;
            Q121=makeQuery(id+"F9.imprint","IMPRINT",FACE,{"disambiguationData":[TD([[makeQuery(id+"F9.imprint","IMPRINT",EDGE,{"derivedFrom":sQuery(id+"F9.wireOp",EDGE,"E11.5.3.0")}),1.0]])]});
            var Q122;
            Q122=makeQuery(id+"F9.imprint","IMPRINT",FACE,{"disambiguationData":[TD([[makeQuery(id+"F9.imprint","IMPRINT",EDGE,{"derivedFrom":sQuery(id+"F9.wireOp",EDGE,"E11.6.3.0")}),1.0]])]});
            var Q123;
            Q123=makeQuery(id+"F9.imprint","IMPRINT",FACE,{"disambiguationData":[TD([[makeQuery(id+"F9.imprint","IMPRINT",EDGE,{"derivedFrom":sQuery(id+"F9.wireOp",EDGE,"E11.6.2.0")}),1.0]])]});
            var Q124;
            Q124=makeQuery(id+"F9.imprint","IMPRINT",FACE,{"disambiguationData":[TD([[makeQuery(id+"F9.imprint","IMPRINT",EDGE,{"derivedFrom":sQuery(id+"F9.wireOp",EDGE,"E11.6.1.0")}),1.0]])]});
            var Q125;
            Q125=makeQuery(id+"F9.imprint","IMPRINT",FACE,{"disambiguationData":[TD([[makeQuery(id+"F9.imprint","IMPRINT",EDGE,{"derivedFrom":sQuery(id+"F9.wireOp",EDGE,"E11.6.0.0")}),1.0]])]});
            var Q126;
            Q126=makeQuery(id+"F9.imprint","IMPRINT",FACE,{"disambiguationData":[TD([[makeQuery(id+"F9.imprint","IMPRINT",EDGE,{"derivedFrom":sQuery(id+"F9.wireOp",EDGE,"E13.1.6.0")}),1.0]])]});
            var Q127;
            Q127=makeQuery(id+"F9.imprint","IMPRINT",FACE,{"disambiguationData":[TD([[makeQuery(id+"F9.imprint","IMPRINT",EDGE,{"derivedFrom":sQuery(id+"F9.wireOp",EDGE,"E13.2.6.0")}),1.0]])]});
            var Q128;
            Q128=makeQuery(id+"F9.imprint","IMPRINT",FACE,{"disambiguationData":[TD([[makeQuery(id+"F9.imprint","IMPRINT",EDGE,{"derivedFrom":sQuery(id+"F9.wireOp",EDGE,"E13.3.6.0")}),1.0]])]});
            var Q129;
            {var subQ0=sQuery(id+"F9.wireOp",EDGE,"E10.4.7.0");var subQ1=sQuery(id+"F0.wireOp",EDGE,"E0.right");var subQ2=makeQuery(id+"F8.opFillet","BLEND_EDGE",EDGE,{"blendedFrom":[makeQuery(id+"F1.opExtrude","CAP_EDGE",EDGE,{"disambiguationData":[OSD([subQ1])],"isStart":false}),makeQuery(id+"F1.opExtrude","CAP_FACE",FACE,{"disambiguationData":[OSD([sQuery(id+"F0.wireOp",EDGE,"E0.bottom"),sQuery(id+"F0.wireOp",EDGE,"E0.top"),sQuery(id+"F0.wireOp",EDGE,"E0.left"),subQ1,sQuery(id+"F0.wireOp",EDGE,"E5.bottom"),sQuery(id+"F0.wireOp",EDGE,"E5.top"),sQuery(id+"F0.wireOp",EDGE,"E5.left"),sQuery(id+"F0.wireOp",EDGE,"E5.right"),sQuery(id+"F0.wireOp",EDGE,"E6"),sQuery(id+"F0.wireOp",EDGE,"E7.MirrorC")])],"isStart":false})],"blendedInto":[makeQuery(id+"F1.opExtrude","CAP_FACE",FACE,{"disambiguationData":[OSD([sQuery(id+"F0.wireOp",EDGE,"E0.bottom"),sQuery(id+"F0.wireOp",EDGE,"E0.top"),sQuery(id+"F0.wireOp",EDGE,"E0.left"),subQ1,sQuery(id+"F0.wireOp",EDGE,"E5.bottom"),sQuery(id+"F0.wireOp",EDGE,"E5.top"),sQuery(id+"F0.wireOp",EDGE,"E5.left"),sQuery(id+"F0.wireOp",EDGE,"E5.right"),sQuery(id+"F0.wireOp",EDGE,"E6"),sQuery(id+"F0.wireOp",EDGE,"E7.MirrorC")])],"isStart":false})]});var subQ3=makeQuery(id+"F9.imprint","INTERSECT",VERTEX,{"disambiguationData":[OD(0.0)],"derivedFrom":[subQ2,subQ0]});Q129=makeQuery(id+"F9.imprint","IMPRINT",FACE,{"disambiguationData":[TD([[makeQuery(id+"F9.imprint","IMPRINT",EDGE,{"disambiguationData":[TD([[subQ3,-1.0]])],"derivedFrom":subQ0}),1.0]])]});}
            extrude(context, id + "F10", {"entities" : qUnion([Q0, Q1, Q2, Q3, Q4, Q5, Q6, Q7, Q8, Q9, Q10, Q11, Q12, Q13, Q14, Q15, Q16, Q17, Q18, Q19, Q20, Q21, Q22, Q23, Q24, Q25, Q26, Q27, Q28, Q29, Q30, Q31, Q32, Q33, Q34, Q35, Q36, Q37, Q38, Q39, Q40, Q41, Q42, Q43, Q44, Q45, Q46, Q47, Q48, Q49, Q50, Q51, Q52, Q53, Q54, Q55, Q56, Q57, Q58, Q59, Q60, Q61, Q62, Q63, Q64, Q65, Q66, Q67, Q68, Q69, Q70, Q71, Q72, Q73, Q74, Q75, Q76, Q77, Q78, Q79, Q80, Q81, Q82, Q83, Q84, Q85, Q86, Q87, Q88, Q89, Q90, Q91, Q92, Q93, Q94, Q95, Q96, Q97, Q98, Q99, Q100, Q101, Q102, Q103, Q104, Q105, Q106, Q107, Q108, Q109, Q110, Q111, Q112, Q113, Q114, Q115, Q116, Q117, Q118, Q119, Q120, Q121, Q122, Q123, Q124, Q125, Q126, Q127, Q128, Q129]), "operationType" : NewBodyOperationType.ADD, "depth" : 1.9 * mm, "offsetDistance" : 25.4 * mm});
        }
    });
